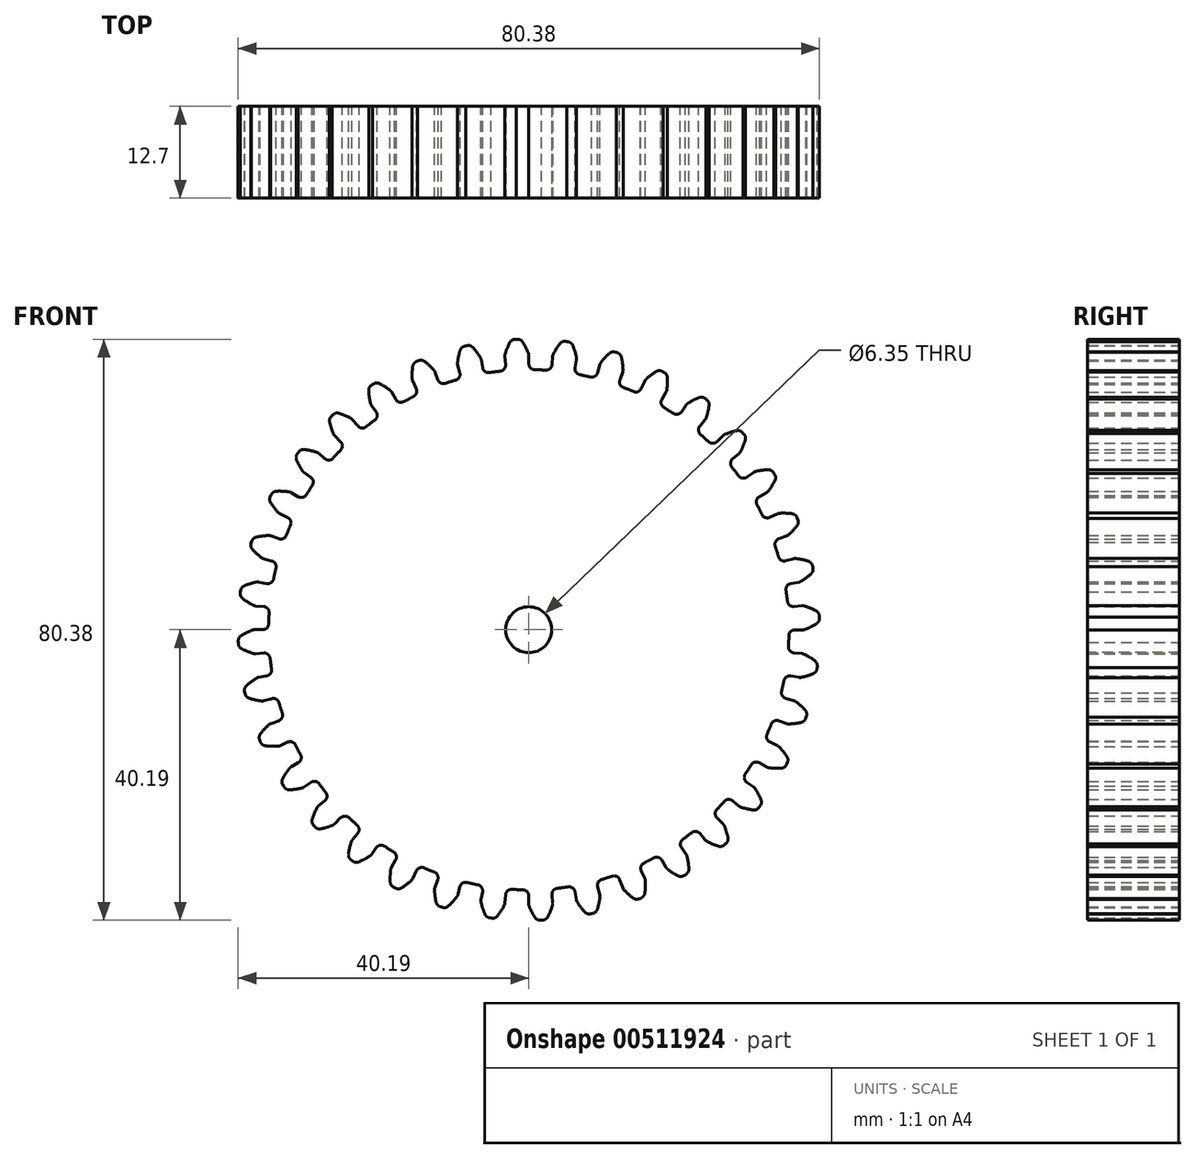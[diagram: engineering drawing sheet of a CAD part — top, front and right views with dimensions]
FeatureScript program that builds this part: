
annotation { "Feature Type Name" : "Feature", "Feature Type Description" : "" }
export const myFeature = defineFeature(function(context is Context, id is Id, definition is map)
    precondition{}
    {
        {
            var Q0;
            Q0=qCreatedBy(makeId("Front.planeOp"),FACE);
            var sketch = newSketch(context, id + "F0", { "sketchPlane" : qUnion([Q0])});
            skArc(sketch, "E0", {"start": v(-3.94, 35.77) * mm, "mid": v(-4.7, 35.68) * mm, "end": v(-5.45, 35.57) * mm});
            skArc(sketch, "E1", {"start": v(-0.05, 38.25) * mm, "mid": v(-0.42, 39.05) * mm, "end": v(-0.85, 39.8) * mm});
            skLineSegment(sketch, "E2", {"start": v(0, 37.94) * mm, "end": v(0, 36.8) * mm});
            skLineSegment(sketch, "E3", {"start": v(-1.58, 40.18) * mm, "end": v(-1.76, 40.18) * mm});
            skLineSegment(sketch, "E4.MirrorCS", {"start": v(-1.93, 40.17) * mm, "end": v(-1.75, 40.18) * mm});
            skArc(sketch, "E5.MirrorCS", {"start": v(-3.28, 38.11) * mm, "mid": v(-2.99, 38.93) * mm, "end": v(-2.62, 39.73) * mm});
            skLineSegment(sketch, "E6.MirrorCS", {"start": v(-3.31, 37.8) * mm, "end": v(-3.21, 36.66) * mm});
            skPoint(sketch, "E7.visualSharp", {"position": v(-3.14, 35.85) * mm});
            skArc(sketch, "E7.filletArc", {"start": v(-3.94, 35.77) * mm, "mid": v(-3.4, 36.07) * mm, "end": v(-3.21, 36.66) * mm});
            skPoint(sketch, "E8.visualSharp", {"position": v(0, 35.98) * mm});
            skArc(sketch, "E8.filletArc", {"start": v(0, 36.8) * mm, "mid": v(0.24, 36.22) * mm, "end": v(0.81, 35.97) * mm});
            skArc(sketch, "E9.filletArc", {"start": v(-1.93, 40.17) * mm, "mid": v(-2.34, 40.04) * mm, "end": v(-2.62, 39.73) * mm});
            skArc(sketch, "E10.filletArc", {"start": v(-0.85, 39.8) * mm, "mid": v(-1.16, 40.1) * mm, "end": v(-1.58, 40.18) * mm});
            skPoint(sketch, "E11.visualSharp", {"position": v(0, 38.1) * mm});
            skArc(sketch, "E11.filletArc", {"start": v(0, 37.94) * mm, "mid": v(0, 38.1) * mm, "end": v(-0.05, 38.25) * mm});
            skPoint(sketch, "E12.visualSharp", {"position": v(-3.33, 37.95) * mm});
            skArc(sketch, "E12.filletArc", {"start": v(-3.28, 38.11) * mm, "mid": v(-3.31, 37.96) * mm, "end": v(-3.31, 37.8) * mm});
            skArc(sketch, "E13.1.0", {"start": v(-10.1, 34.54) * mm, "mid": v(-9.6, 34.93) * mm, "end": v(-9.53, 35.55) * mm});
            skLineSegment(sketch, "E13.1.1", {"start": v(-9.83, 36.65) * mm, "end": v(-9.53, 35.55) * mm});
            skArc(sketch, "E13.1.2", {"start": v(-9.85, 36.96) * mm, "mid": v(-9.85, 36.8) * mm, "end": v(-9.83, 36.65) * mm});
            skArc(sketch, "E13.1.3", {"start": v(-9.85, 36.96) * mm, "mid": v(-9.7, 37.82) * mm, "end": v(-9.48, 38.67) * mm});
            skArc(sketch, "E13.1.4", {"start": v(-8.88, 39.22) * mm, "mid": v(-9.25, 39.03) * mm, "end": v(-9.48, 38.67) * mm});
            skLineSegment(sketch, "E13.1.5", {"start": v(-8.88, 39.22) * mm, "end": v(-8.7, 39.26) * mm});
            skLineSegment(sketch, "E13.1.6", {"start": v(-8.53, 39.3) * mm, "end": v(-8.7, 39.26) * mm});
            skArc(sketch, "E13.1.7", {"start": v(-7.75, 39.05) * mm, "mid": v(-8.1, 39.28) * mm, "end": v(-8.53, 39.3) * mm});
            skArc(sketch, "E13.1.8", {"start": v(-6.7, 37.66) * mm, "mid": v(-7.2, 38.38) * mm, "end": v(-7.75, 39.05) * mm});
            skArc(sketch, "E13.1.9", {"start": v(-6.58, 37.37) * mm, "mid": v(-6.62, 37.52) * mm, "end": v(-6.7, 37.66) * mm});
            skLineSegment(sketch, "E13.1.10", {"start": v(-6.58, 37.37) * mm, "end": v(-6.39, 36.24) * mm});
            skArc(sketch, "E13.1.11", {"start": v(-6.39, 36.24) * mm, "mid": v(-6.06, 35.71) * mm, "end": v(-5.45, 35.57) * mm});
            skArc(sketch, "E13.2.0", {"start": v(-15.94, 32.26) * mm, "mid": v(-15.52, 32.73) * mm, "end": v(-15.56, 33.35) * mm});
            skLineSegment(sketch, "E13.2.1", {"start": v(-16.04, 34.38) * mm, "end": v(-15.56, 33.35) * mm});
            skArc(sketch, "E13.2.2", {"start": v(-16.12, 34.7) * mm, "mid": v(-16.1, 34.53) * mm, "end": v(-16.04, 34.38) * mm});
            skArc(sketch, "E13.2.3", {"start": v(-16.12, 34.7) * mm, "mid": v(-16.13, 35.56) * mm, "end": v(-16.05, 36.43) * mm});
            skArc(sketch, "E13.2.4", {"start": v(-15.55, 37.09) * mm, "mid": v(-15.89, 36.83) * mm, "end": v(-16.05, 36.43) * mm});
            skLineSegment(sketch, "E13.2.5", {"start": v(-15.55, 37.09) * mm, "end": v(-15.39, 37.16) * mm});
            skLineSegment(sketch, "E13.2.6", {"start": v(-15.23, 37.22) * mm, "end": v(-15.4, 37.16) * mm});
            skArc(sketch, "E13.2.7", {"start": v(-14.41, 37.11) * mm, "mid": v(-14.8, 37.28) * mm, "end": v(-15.23, 37.22) * mm});
            skArc(sketch, "E13.2.8", {"start": v(-13.13, 35.93) * mm, "mid": v(-13.75, 36.55) * mm, "end": v(-14.41, 37.11) * mm});
            skArc(sketch, "E13.2.9", {"start": v(-12.97, 35.66) * mm, "mid": v(-13.04, 35.8) * mm, "end": v(-13.13, 35.93) * mm});
            skLineSegment(sketch, "E13.2.10", {"start": v(-12.97, 35.66) * mm, "end": v(-12.58, 34.58) * mm});
            skArc(sketch, "E13.2.11", {"start": v(-12.58, 34.58) * mm, "mid": v(-12.17, 34.12) * mm, "end": v(-11.54, 34.08) * mm});
            skArc(sketch, "E13.3.0", {"start": v(-21.3, 29) * mm, "mid": v(-20.97, 29.54) * mm, "end": v(-21.11, 30.15) * mm});
            skLineSegment(sketch, "E13.3.1", {"start": v(-21.77, 31.08) * mm, "end": v(-21.11, 30.15) * mm});
            skArc(sketch, "E13.3.2", {"start": v(-21.9, 31.37) * mm, "mid": v(-21.85, 31.21) * mm, "end": v(-21.77, 31.08) * mm});
            skArc(sketch, "E13.3.3", {"start": v(-21.9, 31.37) * mm, "mid": v(-22.06, 32.22) * mm, "end": v(-22.13, 33.1) * mm});
            skArc(sketch, "E13.3.4", {"start": v(-21.76, 33.82) * mm, "mid": v(-22.04, 33.5) * mm, "end": v(-22.13, 33.1) * mm});
            skLineSegment(sketch, "E13.3.5", {"start": v(-21.76, 33.82) * mm, "end": v(-21.6, 33.92) * mm});
            skLineSegment(sketch, "E13.3.6", {"start": v(-21.46, 34.01) * mm, "end": v(-21.6, 33.92) * mm});
            skArc(sketch, "E13.3.7", {"start": v(-20.64, 34.05) * mm, "mid": v(-21.05, 34.14) * mm, "end": v(-21.46, 34.01) * mm});
            skArc(sketch, "E13.3.8", {"start": v(-19.17, 33.1) * mm, "mid": v(-19.88, 33.6) * mm, "end": v(-20.64, 34.05) * mm});
            skArc(sketch, "E13.3.9", {"start": v(-18.96, 32.86) * mm, "mid": v(-19.06, 33) * mm, "end": v(-19.17, 33.1) * mm});
            skLineSegment(sketch, "E13.3.10", {"start": v(-18.96, 32.86) * mm, "end": v(-18.4, 31.87) * mm});
            skArc(sketch, "E13.3.11", {"start": v(-18.4, 31.87) * mm, "mid": v(-17.9, 31.49) * mm, "end": v(-17.29, 31.56) * mm});
            skArc(sketch, "E13.4.0", {"start": v(-26.01, 24.86) * mm, "mid": v(-25.78, 25.45) * mm, "end": v(-26.03, 26.02) * mm});
            skLineSegment(sketch, "E13.4.1", {"start": v(-26.83, 26.82) * mm, "end": v(-26.03, 26.02) * mm});
            skArc(sketch, "E13.4.2", {"start": v(-27.01, 27.09) * mm, "mid": v(-26.94, 26.95) * mm, "end": v(-26.83, 26.82) * mm});
            skArc(sketch, "E13.4.3", {"start": v(-27.01, 27.09) * mm, "mid": v(-27.32, 27.9) * mm, "end": v(-27.54, 28.75) * mm});
            skArc(sketch, "E13.4.4", {"start": v(-27.3, 29.53) * mm, "mid": v(-27.53, 29.17) * mm, "end": v(-27.54, 28.75) * mm});
            skLineSegment(sketch, "E13.4.5", {"start": v(-27.3, 29.53) * mm, "end": v(-27.17, 29.65) * mm});
            skLineSegment(sketch, "E13.4.6", {"start": v(-27.04, 29.77) * mm, "end": v(-27.17, 29.65) * mm});
            skArc(sketch, "E13.4.7", {"start": v(-26.24, 29.94) * mm, "mid": v(-26.66, 29.96) * mm, "end": v(-27.04, 29.77) * mm});
            skArc(sketch, "E13.4.8", {"start": v(-24.63, 29.27) * mm, "mid": v(-25.42, 29.64) * mm, "end": v(-26.24, 29.94) * mm});
            skArc(sketch, "E13.4.9", {"start": v(-24.38, 29.07) * mm, "mid": v(-24.5, 29.18) * mm, "end": v(-24.63, 29.27) * mm});
            skLineSegment(sketch, "E13.4.10", {"start": v(-24.38, 29.07) * mm, "end": v(-23.65, 28.2) * mm});
            skArc(sketch, "E13.4.11", {"start": v(-23.65, 28.2) * mm, "mid": v(-23.1, 27.9) * mm, "end": v(-22.5, 28.08) * mm});
            skArc(sketch, "E13.5.0", {"start": v(-29.93, 19.97) * mm, "mid": v(-29.8, 20.58) * mm, "end": v(-30.15, 21.1) * mm});
            skLineSegment(sketch, "E13.5.1", {"start": v(-31.08, 21.76) * mm, "end": v(-30.15, 21.1) * mm});
            skArc(sketch, "E13.5.2", {"start": v(-31.3, 21.98) * mm, "mid": v(-31.2, 21.86) * mm, "end": v(-31.08, 21.76) * mm});
            skArc(sketch, "E13.5.3", {"start": v(-31.3, 21.98) * mm, "mid": v(-31.75, 22.74) * mm, "end": v(-32.12, 23.53) * mm});
            skArc(sketch, "E13.5.4", {"start": v(-32.01, 24.34) * mm, "mid": v(-32.17, 23.95) * mm, "end": v(-32.12, 23.53) * mm});
            skLineSegment(sketch, "E13.5.5", {"start": v(-32.01, 24.34) * mm, "end": v(-31.9, 24.48) * mm});
            skLineSegment(sketch, "E13.5.6", {"start": v(-31.8, 24.62) * mm, "end": v(-31.9, 24.48) * mm});
            skArc(sketch, "E13.5.7", {"start": v(-31.04, 24.93) * mm, "mid": v(-31.46, 24.88) * mm, "end": v(-31.8, 24.62) * mm});
            skArc(sketch, "E13.5.8", {"start": v(-29.34, 24.55) * mm, "mid": v(-30.18, 24.78) * mm, "end": v(-31.04, 24.93) * mm});
            skArc(sketch, "E13.5.9", {"start": v(-29.06, 24.4) * mm, "mid": v(-29.2, 24.49) * mm, "end": v(-29.34, 24.55) * mm});
            skLineSegment(sketch, "E13.5.10", {"start": v(-29.06, 24.4) * mm, "end": v(-28.2, 23.66) * mm});
            skArc(sketch, "E13.5.11", {"start": v(-28.2, 23.66) * mm, "mid": v(-27.6, 23.47) * mm, "end": v(-27.04, 23.74) * mm});
            skArc(sketch, "E13.6.0", {"start": v(-32.95, 14.47) * mm, "mid": v(-32.93, 15.1) * mm, "end": v(-33.36, 15.55) * mm});
            skLineSegment(sketch, "E13.6.1", {"start": v(-34.4, 16.03) * mm, "end": v(-33.36, 15.55) * mm});
            skArc(sketch, "E13.6.2", {"start": v(-34.65, 16.21) * mm, "mid": v(-34.53, 16.1) * mm, "end": v(-34.4, 16.03) * mm});
            skArc(sketch, "E13.6.3", {"start": v(-34.65, 16.21) * mm, "mid": v(-35.21, 16.88) * mm, "end": v(-35.71, 17.6) * mm});
            skArc(sketch, "E13.6.4", {"start": v(-35.75, 18.41) * mm, "mid": v(-35.84, 18) * mm, "end": v(-35.71, 17.6) * mm});
            skLineSegment(sketch, "E13.6.5", {"start": v(-35.75, 18.41) * mm, "end": v(-35.67, 18.57) * mm});
            skLineSegment(sketch, "E13.6.6", {"start": v(-35.59, 18.73) * mm, "end": v(-35.67, 18.57) * mm});
            skArc(sketch, "E13.6.7", {"start": v(-34.9, 19.16) * mm, "mid": v(-35.3, 19.04) * mm, "end": v(-35.59, 18.73) * mm});
            skArc(sketch, "E13.6.8", {"start": v(-33.16, 19.08) * mm, "mid": v(-34.02, 19.16) * mm, "end": v(-34.9, 19.16) * mm});
            skArc(sketch, "E13.6.9", {"start": v(-32.85, 18.98) * mm, "mid": v(-33, 19.04) * mm, "end": v(-33.16, 19.08) * mm});
            skLineSegment(sketch, "E13.6.10", {"start": v(-32.85, 18.98) * mm, "end": v(-31.87, 18.4) * mm});
            skArc(sketch, "E13.6.11", {"start": v(-31.87, 18.4) * mm, "mid": v(-31.25, 18.32) * mm, "end": v(-30.75, 18.69) * mm});
            skArc(sketch, "E13.7.0", {"start": v(-34.96, 8.53) * mm, "mid": v(-35.05, 9.15) * mm, "end": v(-35.55, 9.52) * mm});
            skLineSegment(sketch, "E13.7.1", {"start": v(-36.65, 9.81) * mm, "end": v(-35.55, 9.52) * mm});
            skArc(sketch, "E13.7.2", {"start": v(-36.94, 9.95) * mm, "mid": v(-36.8, 9.87) * mm, "end": v(-36.65, 9.81) * mm});
            skArc(sketch, "E13.7.3", {"start": v(-36.94, 9.95) * mm, "mid": v(-37.6, 10.5) * mm, "end": v(-38.23, 11.12) * mm});
            skArc(sketch, "E13.7.4", {"start": v(-38.4, 11.92) * mm, "mid": v(-38.42, 11.5) * mm, "end": v(-38.23, 11.12) * mm});
            skLineSegment(sketch, "E13.7.5", {"start": v(-38.4, 11.92) * mm, "end": v(-38.36, 12.1) * mm});
            skLineSegment(sketch, "E13.7.6", {"start": v(-38.3, 12.26) * mm, "end": v(-38.36, 12.1) * mm});
            skArc(sketch, "E13.7.7", {"start": v(-37.7, 12.81) * mm, "mid": v(-38.07, 12.62) * mm, "end": v(-38.3, 12.26) * mm});
            skArc(sketch, "E13.7.8", {"start": v(-35.97, 13.03) * mm, "mid": v(-36.83, 12.96) * mm, "end": v(-37.7, 12.81) * mm});
            skArc(sketch, "E13.7.9", {"start": v(-35.65, 12.98) * mm, "mid": v(-35.8, 13.02) * mm, "end": v(-35.97, 13.03) * mm});
            skLineSegment(sketch, "E13.7.10", {"start": v(-35.65, 12.98) * mm, "end": v(-34.58, 12.6) * mm});
            skArc(sketch, "E13.7.11", {"start": v(-34.58, 12.6) * mm, "mid": v(-33.96, 12.61) * mm, "end": v(-33.53, 13.07) * mm});
            skArc(sketch, "E13.8.0", {"start": v(-35.9, 2.33) * mm, "mid": v(-36.1, 2.92) * mm, "end": v(-36.66, 3.2) * mm});
            skLineSegment(sketch, "E13.8.1", {"start": v(-37.8, 3.3) * mm, "end": v(-36.66, 3.2) * mm});
            skArc(sketch, "E13.8.2", {"start": v(-38.1, 3.39) * mm, "mid": v(-37.96, 3.33) * mm, "end": v(-37.8, 3.3) * mm});
            skArc(sketch, "E13.8.3", {"start": v(-38.1, 3.39) * mm, "mid": v(-38.86, 3.82) * mm, "end": v(-39.58, 4.32) * mm});
            skArc(sketch, "E13.8.4", {"start": v(-39.9, 5.07) * mm, "mid": v(-39.84, 4.65) * mm, "end": v(-39.58, 4.32) * mm});
            skLineSegment(sketch, "E13.8.5", {"start": v(-39.9, 5.07) * mm, "end": v(-39.87, 5.25) * mm});
            skLineSegment(sketch, "E13.8.6", {"start": v(-39.85, 5.43) * mm, "end": v(-39.87, 5.25) * mm});
            skArc(sketch, "E13.8.7", {"start": v(-39.35, 6.07) * mm, "mid": v(-39.68, 5.82) * mm, "end": v(-39.85, 5.43) * mm});
            skArc(sketch, "E13.8.8", {"start": v(-37.68, 6.6) * mm, "mid": v(-38.53, 6.37) * mm, "end": v(-39.35, 6.07) * mm});
            skArc(sketch, "E13.8.9", {"start": v(-37.36, 6.6) * mm, "mid": v(-37.52, 6.6) * mm, "end": v(-37.68, 6.6) * mm});
            skLineSegment(sketch, "E13.8.10", {"start": v(-37.36, 6.6) * mm, "end": v(-36.24, 6.4) * mm});
            skArc(sketch, "E13.8.11", {"start": v(-36.24, 6.4) * mm, "mid": v(-35.63, 6.52) * mm, "end": v(-35.29, 7.04) * mm});
            skArc(sketch, "E13.9.0", {"start": v(-35.77, -3.94) * mm, "mid": v(-36.07, -3.4) * mm, "end": v(-36.66, -3.21) * mm});
            skLineSegment(sketch, "E13.9.1", {"start": v(-37.8, -3.31) * mm, "end": v(-36.66, -3.21) * mm});
            skArc(sketch, "E13.9.2", {"start": v(-38.11, -3.28) * mm, "mid": v(-37.96, -3.31) * mm, "end": v(-37.8, -3.31) * mm});
            skArc(sketch, "E13.9.3", {"start": v(-38.11, -3.28) * mm, "mid": v(-38.93, -2.99) * mm, "end": v(-39.73, -2.62) * mm});
            skArc(sketch, "E13.9.4", {"start": v(-40.17, -1.93) * mm, "mid": v(-40.04, -2.34) * mm, "end": v(-39.73, -2.62) * mm});
            skLineSegment(sketch, "E13.9.5", {"start": v(-40.17, -1.93) * mm, "end": v(-40.18, -1.75) * mm});
            skLineSegment(sketch, "E13.9.6", {"start": v(-40.18, -1.58) * mm, "end": v(-40.18, -1.76) * mm});
            skArc(sketch, "E13.9.7", {"start": v(-39.8, -0.85) * mm, "mid": v(-40.1, -1.16) * mm, "end": v(-40.18, -1.58) * mm});
            skArc(sketch, "E13.9.8", {"start": v(-38.25, -0.05) * mm, "mid": v(-39.05, -0.42) * mm, "end": v(-39.8, -0.85) * mm});
            skArc(sketch, "E13.9.9", {"start": v(-37.94, 0) * mm, "mid": v(-38.1, 0) * mm, "end": v(-38.25, -0.05) * mm});
            skLineSegment(sketch, "E13.9.10", {"start": v(-37.94, 0) * mm, "end": v(-36.8, 0) * mm});
            skArc(sketch, "E13.9.11", {"start": v(-36.8, 0) * mm, "mid": v(-36.22, 0.24) * mm, "end": v(-35.97, 0.81) * mm});
            skArc(sketch, "E13.10.0", {"start": v(-34.54, -10.1) * mm, "mid": v(-34.93, -9.6) * mm, "end": v(-35.55, -9.53) * mm});
            skLineSegment(sketch, "E13.10.1", {"start": v(-36.65, -9.83) * mm, "end": v(-35.55, -9.53) * mm});
            skArc(sketch, "E13.10.2", {"start": v(-36.96, -9.85) * mm, "mid": v(-36.8, -9.85) * mm, "end": v(-36.65, -9.83) * mm});
            skArc(sketch, "E13.10.3", {"start": v(-36.96, -9.85) * mm, "mid": v(-37.82, -9.7) * mm, "end": v(-38.67, -9.48) * mm});
            skArc(sketch, "E13.10.4", {"start": v(-39.22, -8.88) * mm, "mid": v(-39.03, -9.25) * mm, "end": v(-38.67, -9.48) * mm});
            skLineSegment(sketch, "E13.10.5", {"start": v(-39.22, -8.88) * mm, "end": v(-39.26, -8.7) * mm});
            skLineSegment(sketch, "E13.10.6", {"start": v(-39.3, -8.53) * mm, "end": v(-39.26, -8.7) * mm});
            skArc(sketch, "E13.10.7", {"start": v(-39.05, -7.75) * mm, "mid": v(-39.28, -8.1) * mm, "end": v(-39.3, -8.53) * mm});
            skArc(sketch, "E13.10.8", {"start": v(-37.66, -6.7) * mm, "mid": v(-38.38, -7.2) * mm, "end": v(-39.05, -7.75) * mm});
            skArc(sketch, "E13.10.9", {"start": v(-37.37, -6.58) * mm, "mid": v(-37.52, -6.62) * mm, "end": v(-37.66, -6.7) * mm});
            skLineSegment(sketch, "E13.10.10", {"start": v(-37.37, -6.58) * mm, "end": v(-36.24, -6.39) * mm});
            skArc(sketch, "E13.10.11", {"start": v(-36.24, -6.39) * mm, "mid": v(-35.71, -6.06) * mm, "end": v(-35.57, -5.45) * mm});
            skArc(sketch, "E13.11.0", {"start": v(-32.26, -15.94) * mm, "mid": v(-32.73, -15.52) * mm, "end": v(-33.35, -15.56) * mm});
            skLineSegment(sketch, "E13.11.1", {"start": v(-34.38, -16.04) * mm, "end": v(-33.35, -15.56) * mm});
            skArc(sketch, "E13.11.2", {"start": v(-34.7, -16.12) * mm, "mid": v(-34.53, -16.1) * mm, "end": v(-34.38, -16.04) * mm});
            skArc(sketch, "E13.11.3", {"start": v(-34.7, -16.12) * mm, "mid": v(-35.56, -16.13) * mm, "end": v(-36.43, -16.05) * mm});
            skArc(sketch, "E13.11.4", {"start": v(-37.09, -15.55) * mm, "mid": v(-36.83, -15.89) * mm, "end": v(-36.43, -16.05) * mm});
            skLineSegment(sketch, "E13.11.5", {"start": v(-37.09, -15.55) * mm, "end": v(-37.16, -15.39) * mm});
            skLineSegment(sketch, "E13.11.6", {"start": v(-37.22, -15.23) * mm, "end": v(-37.16, -15.4) * mm});
            skArc(sketch, "E13.11.7", {"start": v(-37.11, -14.41) * mm, "mid": v(-37.28, -14.8) * mm, "end": v(-37.22, -15.23) * mm});
            skArc(sketch, "E13.11.8", {"start": v(-35.93, -13.13) * mm, "mid": v(-36.55, -13.75) * mm, "end": v(-37.11, -14.41) * mm});
            skArc(sketch, "E13.11.9", {"start": v(-35.66, -12.97) * mm, "mid": v(-35.8, -13.04) * mm, "end": v(-35.93, -13.13) * mm});
            skLineSegment(sketch, "E13.11.10", {"start": v(-35.66, -12.97) * mm, "end": v(-34.58, -12.58) * mm});
            skArc(sketch, "E13.11.11", {"start": v(-34.58, -12.58) * mm, "mid": v(-34.12, -12.17) * mm, "end": v(-34.08, -11.54) * mm});
            skArc(sketch, "E13.12.0", {"start": v(-29, -21.3) * mm, "mid": v(-29.54, -20.97) * mm, "end": v(-30.15, -21.11) * mm});
            skLineSegment(sketch, "E13.12.1", {"start": v(-31.08, -21.77) * mm, "end": v(-30.15, -21.11) * mm});
            skArc(sketch, "E13.12.2", {"start": v(-31.37, -21.9) * mm, "mid": v(-31.21, -21.85) * mm, "end": v(-31.08, -21.77) * mm});
            skArc(sketch, "E13.12.3", {"start": v(-31.37, -21.9) * mm, "mid": v(-32.22, -22.06) * mm, "end": v(-33.1, -22.13) * mm});
            skArc(sketch, "E13.12.4", {"start": v(-33.82, -21.76) * mm, "mid": v(-33.5, -22.04) * mm, "end": v(-33.1, -22.13) * mm});
            skLineSegment(sketch, "E13.12.5", {"start": v(-33.82, -21.76) * mm, "end": v(-33.92, -21.6) * mm});
            skLineSegment(sketch, "E13.12.6", {"start": v(-34.01, -21.46) * mm, "end": v(-33.92, -21.6) * mm});
            skArc(sketch, "E13.12.7", {"start": v(-34.05, -20.64) * mm, "mid": v(-34.14, -21.05) * mm, "end": v(-34.01, -21.46) * mm});
            skArc(sketch, "E13.12.8", {"start": v(-33.1, -19.17) * mm, "mid": v(-33.6, -19.88) * mm, "end": v(-34.05, -20.64) * mm});
            skArc(sketch, "E13.12.9", {"start": v(-32.86, -18.96) * mm, "mid": v(-33, -19.06) * mm, "end": v(-33.1, -19.17) * mm});
            skLineSegment(sketch, "E13.12.10", {"start": v(-32.86, -18.96) * mm, "end": v(-31.87, -18.4) * mm});
            skArc(sketch, "E13.12.11", {"start": v(-31.87, -18.4) * mm, "mid": v(-31.49, -17.9) * mm, "end": v(-31.56, -17.29) * mm});
            skArc(sketch, "E13.13.0", {"start": v(-24.86, -26.01) * mm, "mid": v(-25.45, -25.78) * mm, "end": v(-26.02, -26.03) * mm});
            skLineSegment(sketch, "E13.13.1", {"start": v(-26.82, -26.83) * mm, "end": v(-26.02, -26.03) * mm});
            skArc(sketch, "E13.13.2", {"start": v(-27.09, -27.01) * mm, "mid": v(-26.95, -26.94) * mm, "end": v(-26.82, -26.83) * mm});
            skArc(sketch, "E13.13.3", {"start": v(-27.09, -27.01) * mm, "mid": v(-27.9, -27.32) * mm, "end": v(-28.75, -27.54) * mm});
            skArc(sketch, "E13.13.4", {"start": v(-29.53, -27.3) * mm, "mid": v(-29.17, -27.53) * mm, "end": v(-28.75, -27.54) * mm});
            skLineSegment(sketch, "E13.13.5", {"start": v(-29.53, -27.3) * mm, "end": v(-29.65, -27.17) * mm});
            skLineSegment(sketch, "E13.13.6", {"start": v(-29.77, -27.04) * mm, "end": v(-29.65, -27.17) * mm});
            skArc(sketch, "E13.13.7", {"start": v(-29.94, -26.24) * mm, "mid": v(-29.96, -26.66) * mm, "end": v(-29.77, -27.04) * mm});
            skArc(sketch, "E13.13.8", {"start": v(-29.27, -24.63) * mm, "mid": v(-29.64, -25.42) * mm, "end": v(-29.94, -26.24) * mm});
            skArc(sketch, "E13.13.9", {"start": v(-29.07, -24.38) * mm, "mid": v(-29.18, -24.5) * mm, "end": v(-29.27, -24.63) * mm});
            skLineSegment(sketch, "E13.13.10", {"start": v(-29.07, -24.38) * mm, "end": v(-28.2, -23.65) * mm});
            skArc(sketch, "E13.13.11", {"start": v(-28.2, -23.65) * mm, "mid": v(-27.9, -23.1) * mm, "end": v(-28.08, -22.5) * mm});
            skArc(sketch, "E13.14.0", {"start": v(-19.97, -29.93) * mm, "mid": v(-20.58, -29.8) * mm, "end": v(-21.1, -30.15) * mm});
            skLineSegment(sketch, "E13.14.1", {"start": v(-21.76, -31.08) * mm, "end": v(-21.1, -30.15) * mm});
            skArc(sketch, "E13.14.2", {"start": v(-21.98, -31.3) * mm, "mid": v(-21.86, -31.2) * mm, "end": v(-21.76, -31.08) * mm});
            skArc(sketch, "E13.14.3", {"start": v(-21.98, -31.3) * mm, "mid": v(-22.74, -31.75) * mm, "end": v(-23.53, -32.12) * mm});
            skArc(sketch, "E13.14.4", {"start": v(-24.34, -32.01) * mm, "mid": v(-23.95, -32.17) * mm, "end": v(-23.53, -32.12) * mm});
            skLineSegment(sketch, "E13.14.5", {"start": v(-24.34, -32.01) * mm, "end": v(-24.48, -31.9) * mm});
            skLineSegment(sketch, "E13.14.6", {"start": v(-24.62, -31.8) * mm, "end": v(-24.48, -31.9) * mm});
            skArc(sketch, "E13.14.7", {"start": v(-24.93, -31.04) * mm, "mid": v(-24.88, -31.46) * mm, "end": v(-24.62, -31.8) * mm});
            skArc(sketch, "E13.14.8", {"start": v(-24.55, -29.34) * mm, "mid": v(-24.78, -30.18) * mm, "end": v(-24.93, -31.04) * mm});
            skArc(sketch, "E13.14.9", {"start": v(-24.4, -29.06) * mm, "mid": v(-24.49, -29.2) * mm, "end": v(-24.55, -29.34) * mm});
            skLineSegment(sketch, "E13.14.10", {"start": v(-24.4, -29.06) * mm, "end": v(-23.66, -28.2) * mm});
            skArc(sketch, "E13.14.11", {"start": v(-23.66, -28.2) * mm, "mid": v(-23.47, -27.6) * mm, "end": v(-23.74, -27.04) * mm});
            skArc(sketch, "E13.15.0", {"start": v(-14.47, -32.95) * mm, "mid": v(-15.1, -32.93) * mm, "end": v(-15.55, -33.36) * mm});
            skLineSegment(sketch, "E13.15.1", {"start": v(-16.03, -34.4) * mm, "end": v(-15.55, -33.36) * mm});
            skArc(sketch, "E13.15.2", {"start": v(-16.21, -34.65) * mm, "mid": v(-16.1, -34.53) * mm, "end": v(-16.03, -34.4) * mm});
            skArc(sketch, "E13.15.3", {"start": v(-16.21, -34.65) * mm, "mid": v(-16.88, -35.21) * mm, "end": v(-17.6, -35.71) * mm});
            skArc(sketch, "E13.15.4", {"start": v(-18.41, -35.75) * mm, "mid": v(-18, -35.84) * mm, "end": v(-17.6, -35.71) * mm});
            skLineSegment(sketch, "E13.15.5", {"start": v(-18.41, -35.75) * mm, "end": v(-18.57, -35.67) * mm});
            skLineSegment(sketch, "E13.15.6", {"start": v(-18.73, -35.59) * mm, "end": v(-18.57, -35.67) * mm});
            skArc(sketch, "E13.15.7", {"start": v(-19.16, -34.9) * mm, "mid": v(-19.04, -35.3) * mm, "end": v(-18.73, -35.59) * mm});
            skArc(sketch, "E13.15.8", {"start": v(-19.08, -33.16) * mm, "mid": v(-19.16, -34.02) * mm, "end": v(-19.16, -34.9) * mm});
            skArc(sketch, "E13.15.9", {"start": v(-18.98, -32.85) * mm, "mid": v(-19.04, -33) * mm, "end": v(-19.08, -33.16) * mm});
            skLineSegment(sketch, "E13.15.10", {"start": v(-18.98, -32.85) * mm, "end": v(-18.4, -31.87) * mm});
            skArc(sketch, "E13.15.11", {"start": v(-18.4, -31.87) * mm, "mid": v(-18.32, -31.25) * mm, "end": v(-18.69, -30.75) * mm});
            skArc(sketch, "E13.16.0", {"start": v(-8.53, -34.96) * mm, "mid": v(-9.15, -35.05) * mm, "end": v(-9.52, -35.55) * mm});
            skLineSegment(sketch, "E13.16.1", {"start": v(-9.81, -36.65) * mm, "end": v(-9.52, -35.55) * mm});
            skArc(sketch, "E13.16.2", {"start": v(-9.95, -36.94) * mm, "mid": v(-9.87, -36.8) * mm, "end": v(-9.81, -36.65) * mm});
            skArc(sketch, "E13.16.3", {"start": v(-9.95, -36.94) * mm, "mid": v(-10.5, -37.6) * mm, "end": v(-11.12, -38.23) * mm});
            skArc(sketch, "E13.16.4", {"start": v(-11.92, -38.4) * mm, "mid": v(-11.5, -38.42) * mm, "end": v(-11.12, -38.23) * mm});
            skLineSegment(sketch, "E13.16.5", {"start": v(-11.92, -38.4) * mm, "end": v(-12.1, -38.36) * mm});
            skLineSegment(sketch, "E13.16.6", {"start": v(-12.26, -38.3) * mm, "end": v(-12.1, -38.36) * mm});
            skArc(sketch, "E13.16.7", {"start": v(-12.81, -37.7) * mm, "mid": v(-12.62, -38.07) * mm, "end": v(-12.26, -38.3) * mm});
            skArc(sketch, "E13.16.8", {"start": v(-13.03, -35.97) * mm, "mid": v(-12.96, -36.83) * mm, "end": v(-12.81, -37.7) * mm});
            skArc(sketch, "E13.16.9", {"start": v(-12.98, -35.65) * mm, "mid": v(-13.02, -35.8) * mm, "end": v(-13.03, -35.97) * mm});
            skLineSegment(sketch, "E13.16.10", {"start": v(-12.98, -35.65) * mm, "end": v(-12.6, -34.58) * mm});
            skArc(sketch, "E13.16.11", {"start": v(-12.6, -34.58) * mm, "mid": v(-12.61, -33.96) * mm, "end": v(-13.07, -33.53) * mm});
            skArc(sketch, "E13.17.0", {"start": v(-2.33, -35.9) * mm, "mid": v(-2.92, -36.1) * mm, "end": v(-3.2, -36.66) * mm});
            skLineSegment(sketch, "E13.17.1", {"start": v(-3.3, -37.8) * mm, "end": v(-3.2, -36.66) * mm});
            skArc(sketch, "E13.17.2", {"start": v(-3.39, -38.1) * mm, "mid": v(-3.33, -37.96) * mm, "end": v(-3.3, -37.8) * mm});
            skArc(sketch, "E13.17.3", {"start": v(-3.39, -38.1) * mm, "mid": v(-3.82, -38.86) * mm, "end": v(-4.32, -39.58) * mm});
            skArc(sketch, "E13.17.4", {"start": v(-5.07, -39.9) * mm, "mid": v(-4.65, -39.84) * mm, "end": v(-4.32, -39.58) * mm});
            skLineSegment(sketch, "E13.17.5", {"start": v(-5.07, -39.9) * mm, "end": v(-5.25, -39.87) * mm});
            skLineSegment(sketch, "E13.17.6", {"start": v(-5.43, -39.85) * mm, "end": v(-5.25, -39.87) * mm});
            skArc(sketch, "E13.17.7", {"start": v(-6.07, -39.35) * mm, "mid": v(-5.82, -39.68) * mm, "end": v(-5.43, -39.85) * mm});
            skArc(sketch, "E13.17.8", {"start": v(-6.6, -37.68) * mm, "mid": v(-6.37, -38.53) * mm, "end": v(-6.07, -39.35) * mm});
            skArc(sketch, "E13.17.9", {"start": v(-6.6, -37.36) * mm, "mid": v(-6.6, -37.52) * mm, "end": v(-6.6, -37.68) * mm});
            skLineSegment(sketch, "E13.17.10", {"start": v(-6.6, -37.36) * mm, "end": v(-6.4, -36.24) * mm});
            skArc(sketch, "E13.17.11", {"start": v(-6.4, -36.24) * mm, "mid": v(-6.52, -35.63) * mm, "end": v(-7.04, -35.29) * mm});
            skArc(sketch, "E13.18.0", {"start": v(3.94, -35.77) * mm, "mid": v(3.4, -36.07) * mm, "end": v(3.21, -36.66) * mm});
            skLineSegment(sketch, "E13.18.1", {"start": v(3.31, -37.8) * mm, "end": v(3.21, -36.66) * mm});
            skArc(sketch, "E13.18.2", {"start": v(3.28, -38.11) * mm, "mid": v(3.31, -37.96) * mm, "end": v(3.31, -37.8) * mm});
            skArc(sketch, "E13.18.3", {"start": v(3.28, -38.11) * mm, "mid": v(2.99, -38.93) * mm, "end": v(2.62, -39.73) * mm});
            skArc(sketch, "E13.18.4", {"start": v(1.93, -40.17) * mm, "mid": v(2.34, -40.04) * mm, "end": v(2.62, -39.73) * mm});
            skLineSegment(sketch, "E13.18.5", {"start": v(1.93, -40.17) * mm, "end": v(1.75, -40.18) * mm});
            skLineSegment(sketch, "E13.18.6", {"start": v(1.58, -40.18) * mm, "end": v(1.76, -40.18) * mm});
            skArc(sketch, "E13.18.7", {"start": v(0.85, -39.8) * mm, "mid": v(1.16, -40.1) * mm, "end": v(1.58, -40.18) * mm});
            skArc(sketch, "E13.18.8", {"start": v(0.05, -38.25) * mm, "mid": v(0.42, -39.05) * mm, "end": v(0.85, -39.8) * mm});
            skArc(sketch, "E13.18.9", {"start": v(0, -37.94) * mm, "mid": v(0, -38.1) * mm, "end": v(0.05, -38.25) * mm});
            skLineSegment(sketch, "E13.18.10", {"start": v(0, -37.94) * mm, "end": v(0, -36.8) * mm});
            skArc(sketch, "E13.18.11", {"start": v(0, -36.8) * mm, "mid": v(-0.24, -36.22) * mm, "end": v(-0.81, -35.97) * mm});
            skArc(sketch, "E13.19.0", {"start": v(10.1, -34.54) * mm, "mid": v(9.6, -34.93) * mm, "end": v(9.53, -35.55) * mm});
            skLineSegment(sketch, "E13.19.1", {"start": v(9.83, -36.65) * mm, "end": v(9.53, -35.55) * mm});
            skArc(sketch, "E13.19.2", {"start": v(9.85, -36.96) * mm, "mid": v(9.85, -36.8) * mm, "end": v(9.83, -36.65) * mm});
            skArc(sketch, "E13.19.3", {"start": v(9.85, -36.96) * mm, "mid": v(9.7, -37.82) * mm, "end": v(9.48, -38.67) * mm});
            skArc(sketch, "E13.19.4", {"start": v(8.88, -39.22) * mm, "mid": v(9.25, -39.03) * mm, "end": v(9.48, -38.67) * mm});
            skLineSegment(sketch, "E13.19.5", {"start": v(8.88, -39.22) * mm, "end": v(8.7, -39.26) * mm});
            skLineSegment(sketch, "E13.19.6", {"start": v(8.53, -39.3) * mm, "end": v(8.7, -39.26) * mm});
            skArc(sketch, "E13.19.7", {"start": v(7.75, -39.05) * mm, "mid": v(8.1, -39.28) * mm, "end": v(8.53, -39.3) * mm});
            skArc(sketch, "E13.19.8", {"start": v(6.7, -37.66) * mm, "mid": v(7.2, -38.38) * mm, "end": v(7.75, -39.05) * mm});
            skArc(sketch, "E13.19.9", {"start": v(6.58, -37.37) * mm, "mid": v(6.62, -37.52) * mm, "end": v(6.7, -37.66) * mm});
            skLineSegment(sketch, "E13.19.10", {"start": v(6.58, -37.37) * mm, "end": v(6.39, -36.24) * mm});
            skArc(sketch, "E13.19.11", {"start": v(6.39, -36.24) * mm, "mid": v(6.06, -35.71) * mm, "end": v(5.45, -35.57) * mm});
            skArc(sketch, "E13.20.0", {"start": v(15.94, -32.26) * mm, "mid": v(15.52, -32.73) * mm, "end": v(15.56, -33.35) * mm});
            skLineSegment(sketch, "E13.20.1", {"start": v(16.04, -34.38) * mm, "end": v(15.56, -33.35) * mm});
            skArc(sketch, "E13.20.2", {"start": v(16.12, -34.7) * mm, "mid": v(16.1, -34.53) * mm, "end": v(16.04, -34.38) * mm});
            skArc(sketch, "E13.20.3", {"start": v(16.12, -34.7) * mm, "mid": v(16.13, -35.56) * mm, "end": v(16.05, -36.43) * mm});
            skArc(sketch, "E13.20.4", {"start": v(15.55, -37.09) * mm, "mid": v(15.89, -36.83) * mm, "end": v(16.05, -36.43) * mm});
            skLineSegment(sketch, "E13.20.5", {"start": v(15.55, -37.09) * mm, "end": v(15.39, -37.16) * mm});
            skLineSegment(sketch, "E13.20.6", {"start": v(15.23, -37.22) * mm, "end": v(15.4, -37.16) * mm});
            skArc(sketch, "E13.20.7", {"start": v(14.41, -37.11) * mm, "mid": v(14.8, -37.28) * mm, "end": v(15.23, -37.22) * mm});
            skArc(sketch, "E13.20.8", {"start": v(13.13, -35.93) * mm, "mid": v(13.75, -36.55) * mm, "end": v(14.41, -37.11) * mm});
            skArc(sketch, "E13.20.9", {"start": v(12.97, -35.66) * mm, "mid": v(13.04, -35.8) * mm, "end": v(13.13, -35.93) * mm});
            skLineSegment(sketch, "E13.20.10", {"start": v(12.97, -35.66) * mm, "end": v(12.58, -34.58) * mm});
            skArc(sketch, "E13.20.11", {"start": v(12.58, -34.58) * mm, "mid": v(12.17, -34.12) * mm, "end": v(11.54, -34.08) * mm});
            skArc(sketch, "E13.21.0", {"start": v(21.3, -29) * mm, "mid": v(20.97, -29.54) * mm, "end": v(21.11, -30.15) * mm});
            skLineSegment(sketch, "E13.21.1", {"start": v(21.77, -31.08) * mm, "end": v(21.11, -30.15) * mm});
            skArc(sketch, "E13.21.2", {"start": v(21.9, -31.37) * mm, "mid": v(21.85, -31.21) * mm, "end": v(21.77, -31.08) * mm});
            skArc(sketch, "E13.21.3", {"start": v(21.9, -31.37) * mm, "mid": v(22.06, -32.22) * mm, "end": v(22.13, -33.1) * mm});
            skArc(sketch, "E13.21.4", {"start": v(21.76, -33.82) * mm, "mid": v(22.04, -33.5) * mm, "end": v(22.13, -33.1) * mm});
            skLineSegment(sketch, "E13.21.5", {"start": v(21.76, -33.82) * mm, "end": v(21.6, -33.92) * mm});
            skLineSegment(sketch, "E13.21.6", {"start": v(21.46, -34.01) * mm, "end": v(21.6, -33.92) * mm});
            skArc(sketch, "E13.21.7", {"start": v(20.64, -34.05) * mm, "mid": v(21.05, -34.14) * mm, "end": v(21.46, -34.01) * mm});
            skArc(sketch, "E13.21.8", {"start": v(19.17, -33.1) * mm, "mid": v(19.88, -33.6) * mm, "end": v(20.64, -34.05) * mm});
            skArc(sketch, "E13.21.9", {"start": v(18.96, -32.86) * mm, "mid": v(19.06, -33) * mm, "end": v(19.17, -33.1) * mm});
            skLineSegment(sketch, "E13.21.10", {"start": v(18.96, -32.86) * mm, "end": v(18.4, -31.87) * mm});
            skArc(sketch, "E13.21.11", {"start": v(18.4, -31.87) * mm, "mid": v(17.9, -31.49) * mm, "end": v(17.29, -31.56) * mm});
            skArc(sketch, "E13.22.0", {"start": v(26.01, -24.86) * mm, "mid": v(25.78, -25.45) * mm, "end": v(26.03, -26.02) * mm});
            skLineSegment(sketch, "E13.22.1", {"start": v(26.83, -26.82) * mm, "end": v(26.03, -26.02) * mm});
            skArc(sketch, "E13.22.2", {"start": v(27.01, -27.09) * mm, "mid": v(26.94, -26.95) * mm, "end": v(26.83, -26.82) * mm});
            skArc(sketch, "E13.22.3", {"start": v(27.01, -27.09) * mm, "mid": v(27.32, -27.9) * mm, "end": v(27.54, -28.75) * mm});
            skArc(sketch, "E13.22.4", {"start": v(27.3, -29.53) * mm, "mid": v(27.53, -29.17) * mm, "end": v(27.54, -28.75) * mm});
            skLineSegment(sketch, "E13.22.5", {"start": v(27.3, -29.53) * mm, "end": v(27.17, -29.65) * mm});
            skLineSegment(sketch, "E13.22.6", {"start": v(27.04, -29.77) * mm, "end": v(27.17, -29.65) * mm});
            skArc(sketch, "E13.22.7", {"start": v(26.24, -29.94) * mm, "mid": v(26.66, -29.96) * mm, "end": v(27.04, -29.77) * mm});
            skArc(sketch, "E13.22.8", {"start": v(24.63, -29.27) * mm, "mid": v(25.42, -29.64) * mm, "end": v(26.24, -29.94) * mm});
            skArc(sketch, "E13.22.9", {"start": v(24.38, -29.07) * mm, "mid": v(24.5, -29.18) * mm, "end": v(24.63, -29.27) * mm});
            skLineSegment(sketch, "E13.22.10", {"start": v(24.38, -29.07) * mm, "end": v(23.65, -28.2) * mm});
            skArc(sketch, "E13.22.11", {"start": v(23.65, -28.2) * mm, "mid": v(23.1, -27.9) * mm, "end": v(22.5, -28.08) * mm});
            skArc(sketch, "E13.23.0", {"start": v(29.93, -19.97) * mm, "mid": v(29.8, -20.58) * mm, "end": v(30.15, -21.1) * mm});
            skLineSegment(sketch, "E13.23.1", {"start": v(31.08, -21.76) * mm, "end": v(30.15, -21.1) * mm});
            skArc(sketch, "E13.23.2", {"start": v(31.3, -21.98) * mm, "mid": v(31.2, -21.86) * mm, "end": v(31.08, -21.76) * mm});
            skArc(sketch, "E13.23.3", {"start": v(31.3, -21.98) * mm, "mid": v(31.75, -22.74) * mm, "end": v(32.12, -23.53) * mm});
            skArc(sketch, "E13.23.4", {"start": v(32.01, -24.34) * mm, "mid": v(32.17, -23.95) * mm, "end": v(32.12, -23.53) * mm});
            skLineSegment(sketch, "E13.23.5", {"start": v(32.01, -24.34) * mm, "end": v(31.9, -24.48) * mm});
            skLineSegment(sketch, "E13.23.6", {"start": v(31.8, -24.62) * mm, "end": v(31.9, -24.48) * mm});
            skArc(sketch, "E13.23.7", {"start": v(31.04, -24.93) * mm, "mid": v(31.46, -24.88) * mm, "end": v(31.8, -24.62) * mm});
            skArc(sketch, "E13.23.8", {"start": v(29.34, -24.55) * mm, "mid": v(30.18, -24.78) * mm, "end": v(31.04, -24.93) * mm});
            skArc(sketch, "E13.23.9", {"start": v(29.06, -24.4) * mm, "mid": v(29.2, -24.49) * mm, "end": v(29.34, -24.55) * mm});
            skLineSegment(sketch, "E13.23.10", {"start": v(29.06, -24.4) * mm, "end": v(28.2, -23.66) * mm});
            skArc(sketch, "E13.23.11", {"start": v(28.2, -23.66) * mm, "mid": v(27.6, -23.47) * mm, "end": v(27.04, -23.74) * mm});
            skArc(sketch, "E13.24.0", {"start": v(32.95, -14.47) * mm, "mid": v(32.93, -15.1) * mm, "end": v(33.36, -15.55) * mm});
            skLineSegment(sketch, "E13.24.1", {"start": v(34.4, -16.03) * mm, "end": v(33.36, -15.55) * mm});
            skArc(sketch, "E13.24.2", {"start": v(34.65, -16.21) * mm, "mid": v(34.53, -16.1) * mm, "end": v(34.4, -16.03) * mm});
            skArc(sketch, "E13.24.3", {"start": v(34.65, -16.21) * mm, "mid": v(35.21, -16.88) * mm, "end": v(35.71, -17.6) * mm});
            skArc(sketch, "E13.24.4", {"start": v(35.75, -18.41) * mm, "mid": v(35.84, -18) * mm, "end": v(35.71, -17.6) * mm});
            skLineSegment(sketch, "E13.24.5", {"start": v(35.75, -18.41) * mm, "end": v(35.67, -18.57) * mm});
            skLineSegment(sketch, "E13.24.6", {"start": v(35.59, -18.73) * mm, "end": v(35.67, -18.57) * mm});
            skArc(sketch, "E13.24.7", {"start": v(34.9, -19.16) * mm, "mid": v(35.3, -19.04) * mm, "end": v(35.59, -18.73) * mm});
            skArc(sketch, "E13.24.8", {"start": v(33.16, -19.08) * mm, "mid": v(34.02, -19.16) * mm, "end": v(34.9, -19.16) * mm});
            skArc(sketch, "E13.24.9", {"start": v(32.85, -18.98) * mm, "mid": v(33, -19.04) * mm, "end": v(33.16, -19.08) * mm});
            skLineSegment(sketch, "E13.24.10", {"start": v(32.85, -18.98) * mm, "end": v(31.87, -18.4) * mm});
            skArc(sketch, "E13.24.11", {"start": v(31.87, -18.4) * mm, "mid": v(31.25, -18.32) * mm, "end": v(30.75, -18.69) * mm});
            skArc(sketch, "E13.25.0", {"start": v(34.96, -8.53) * mm, "mid": v(35.05, -9.15) * mm, "end": v(35.55, -9.52) * mm});
            skLineSegment(sketch, "E13.25.1", {"start": v(36.65, -9.81) * mm, "end": v(35.55, -9.52) * mm});
            skArc(sketch, "E13.25.2", {"start": v(36.94, -9.95) * mm, "mid": v(36.8, -9.87) * mm, "end": v(36.65, -9.81) * mm});
            skArc(sketch, "E13.25.3", {"start": v(36.94, -9.95) * mm, "mid": v(37.6, -10.5) * mm, "end": v(38.23, -11.12) * mm});
            skArc(sketch, "E13.25.4", {"start": v(38.4, -11.92) * mm, "mid": v(38.42, -11.5) * mm, "end": v(38.23, -11.12) * mm});
            skLineSegment(sketch, "E13.25.5", {"start": v(38.4, -11.92) * mm, "end": v(38.36, -12.1) * mm});
            skLineSegment(sketch, "E13.25.6", {"start": v(38.3, -12.26) * mm, "end": v(38.36, -12.1) * mm});
            skArc(sketch, "E13.25.7", {"start": v(37.7, -12.81) * mm, "mid": v(38.07, -12.62) * mm, "end": v(38.3, -12.26) * mm});
            skArc(sketch, "E13.25.8", {"start": v(35.97, -13.03) * mm, "mid": v(36.83, -12.96) * mm, "end": v(37.7, -12.81) * mm});
            skArc(sketch, "E13.25.9", {"start": v(35.65, -12.98) * mm, "mid": v(35.8, -13.02) * mm, "end": v(35.97, -13.03) * mm});
            skLineSegment(sketch, "E13.25.10", {"start": v(35.65, -12.98) * mm, "end": v(34.58, -12.6) * mm});
            skArc(sketch, "E13.25.11", {"start": v(34.58, -12.6) * mm, "mid": v(33.96, -12.61) * mm, "end": v(33.53, -13.07) * mm});
            skArc(sketch, "E13.26.0", {"start": v(35.9, -2.33) * mm, "mid": v(36.1, -2.92) * mm, "end": v(36.66, -3.2) * mm});
            skLineSegment(sketch, "E13.26.1", {"start": v(37.8, -3.3) * mm, "end": v(36.66, -3.2) * mm});
            skArc(sketch, "E13.26.2", {"start": v(38.1, -3.39) * mm, "mid": v(37.96, -3.33) * mm, "end": v(37.8, -3.3) * mm});
            skArc(sketch, "E13.26.3", {"start": v(38.1, -3.39) * mm, "mid": v(38.86, -3.82) * mm, "end": v(39.58, -4.32) * mm});
            skArc(sketch, "E13.26.4", {"start": v(39.9, -5.07) * mm, "mid": v(39.84, -4.65) * mm, "end": v(39.58, -4.32) * mm});
            skLineSegment(sketch, "E13.26.5", {"start": v(39.9, -5.07) * mm, "end": v(39.87, -5.25) * mm});
            skLineSegment(sketch, "E13.26.6", {"start": v(39.85, -5.43) * mm, "end": v(39.87, -5.25) * mm});
            skArc(sketch, "E13.26.7", {"start": v(39.35, -6.07) * mm, "mid": v(39.68, -5.82) * mm, "end": v(39.85, -5.43) * mm});
            skArc(sketch, "E13.26.8", {"start": v(37.68, -6.6) * mm, "mid": v(38.53, -6.37) * mm, "end": v(39.35, -6.07) * mm});
            skArc(sketch, "E13.26.9", {"start": v(37.36, -6.6) * mm, "mid": v(37.52, -6.6) * mm, "end": v(37.68, -6.6) * mm});
            skLineSegment(sketch, "E13.26.10", {"start": v(37.36, -6.6) * mm, "end": v(36.24, -6.4) * mm});
            skArc(sketch, "E13.26.11", {"start": v(36.24, -6.4) * mm, "mid": v(35.63, -6.52) * mm, "end": v(35.29, -7.04) * mm});
            skArc(sketch, "E13.27.0", {"start": v(35.77, 3.94) * mm, "mid": v(36.07, 3.4) * mm, "end": v(36.66, 3.21) * mm});
            skLineSegment(sketch, "E13.27.1", {"start": v(37.8, 3.31) * mm, "end": v(36.66, 3.21) * mm});
            skArc(sketch, "E13.27.2", {"start": v(38.11, 3.28) * mm, "mid": v(37.96, 3.31) * mm, "end": v(37.8, 3.31) * mm});
            skArc(sketch, "E13.27.3", {"start": v(38.11, 3.28) * mm, "mid": v(38.93, 2.99) * mm, "end": v(39.73, 2.62) * mm});
            skArc(sketch, "E13.27.4", {"start": v(40.17, 1.93) * mm, "mid": v(40.04, 2.34) * mm, "end": v(39.73, 2.62) * mm});
            skLineSegment(sketch, "E13.27.5", {"start": v(40.17, 1.93) * mm, "end": v(40.18, 1.75) * mm});
            skLineSegment(sketch, "E13.27.6", {"start": v(40.18, 1.58) * mm, "end": v(40.18, 1.76) * mm});
            skArc(sketch, "E13.27.7", {"start": v(39.8, 0.85) * mm, "mid": v(40.1, 1.16) * mm, "end": v(40.18, 1.58) * mm});
            skArc(sketch, "E13.27.8", {"start": v(38.25, 0.05) * mm, "mid": v(39.05, 0.42) * mm, "end": v(39.8, 0.85) * mm});
            skArc(sketch, "E13.27.9", {"start": v(37.94, 0) * mm, "mid": v(38.1, 0) * mm, "end": v(38.25, 0.05) * mm});
            skLineSegment(sketch, "E13.27.10", {"start": v(37.94, 0) * mm, "end": v(36.8, 0) * mm});
            skArc(sketch, "E13.27.11", {"start": v(36.8, 0) * mm, "mid": v(36.22, -0.24) * mm, "end": v(35.97, -0.81) * mm});
            skArc(sketch, "E13.28.0", {"start": v(34.54, 10.1) * mm, "mid": v(34.93, 9.6) * mm, "end": v(35.55, 9.53) * mm});
            skLineSegment(sketch, "E13.28.1", {"start": v(36.65, 9.83) * mm, "end": v(35.55, 9.53) * mm});
            skArc(sketch, "E13.28.2", {"start": v(36.96, 9.85) * mm, "mid": v(36.8, 9.85) * mm, "end": v(36.65, 9.83) * mm});
            skArc(sketch, "E13.28.3", {"start": v(36.96, 9.85) * mm, "mid": v(37.82, 9.7) * mm, "end": v(38.67, 9.48) * mm});
            skArc(sketch, "E13.28.4", {"start": v(39.22, 8.88) * mm, "mid": v(39.03, 9.25) * mm, "end": v(38.67, 9.48) * mm});
            skLineSegment(sketch, "E13.28.5", {"start": v(39.22, 8.88) * mm, "end": v(39.26, 8.7) * mm});
            skLineSegment(sketch, "E13.28.6", {"start": v(39.3, 8.53) * mm, "end": v(39.26, 8.7) * mm});
            skArc(sketch, "E13.28.7", {"start": v(39.05, 7.75) * mm, "mid": v(39.28, 8.1) * mm, "end": v(39.3, 8.53) * mm});
            skArc(sketch, "E13.28.8", {"start": v(37.66, 6.7) * mm, "mid": v(38.38, 7.2) * mm, "end": v(39.05, 7.75) * mm});
            skArc(sketch, "E13.28.9", {"start": v(37.37, 6.58) * mm, "mid": v(37.52, 6.62) * mm, "end": v(37.66, 6.7) * mm});
            skLineSegment(sketch, "E13.28.10", {"start": v(37.37, 6.58) * mm, "end": v(36.24, 6.39) * mm});
            skArc(sketch, "E13.28.11", {"start": v(36.24, 6.39) * mm, "mid": v(35.71, 6.06) * mm, "end": v(35.57, 5.45) * mm});
            skArc(sketch, "E13.29.0", {"start": v(32.26, 15.94) * mm, "mid": v(32.73, 15.52) * mm, "end": v(33.35, 15.56) * mm});
            skLineSegment(sketch, "E13.29.1", {"start": v(34.38, 16.04) * mm, "end": v(33.35, 15.56) * mm});
            skArc(sketch, "E13.29.2", {"start": v(34.7, 16.12) * mm, "mid": v(34.53, 16.1) * mm, "end": v(34.38, 16.04) * mm});
            skArc(sketch, "E13.29.3", {"start": v(34.7, 16.12) * mm, "mid": v(35.56, 16.13) * mm, "end": v(36.43, 16.05) * mm});
            skArc(sketch, "E13.29.4", {"start": v(37.09, 15.55) * mm, "mid": v(36.83, 15.89) * mm, "end": v(36.43, 16.05) * mm});
            skLineSegment(sketch, "E13.29.5", {"start": v(37.09, 15.55) * mm, "end": v(37.16, 15.39) * mm});
            skLineSegment(sketch, "E13.29.6", {"start": v(37.22, 15.23) * mm, "end": v(37.16, 15.4) * mm});
            skArc(sketch, "E13.29.7", {"start": v(37.11, 14.41) * mm, "mid": v(37.28, 14.8) * mm, "end": v(37.22, 15.23) * mm});
            skArc(sketch, "E13.29.8", {"start": v(35.93, 13.13) * mm, "mid": v(36.55, 13.75) * mm, "end": v(37.11, 14.41) * mm});
            skArc(sketch, "E13.29.9", {"start": v(35.66, 12.97) * mm, "mid": v(35.8, 13.04) * mm, "end": v(35.93, 13.13) * mm});
            skLineSegment(sketch, "E13.29.10", {"start": v(35.66, 12.97) * mm, "end": v(34.58, 12.58) * mm});
            skArc(sketch, "E13.29.11", {"start": v(34.58, 12.58) * mm, "mid": v(34.12, 12.17) * mm, "end": v(34.08, 11.54) * mm});
            skArc(sketch, "E13.30.0", {"start": v(29, 21.3) * mm, "mid": v(29.54, 20.97) * mm, "end": v(30.15, 21.11) * mm});
            skLineSegment(sketch, "E13.30.1", {"start": v(31.08, 21.77) * mm, "end": v(30.15, 21.11) * mm});
            skArc(sketch, "E13.30.2", {"start": v(31.37, 21.9) * mm, "mid": v(31.21, 21.85) * mm, "end": v(31.08, 21.77) * mm});
            skArc(sketch, "E13.30.3", {"start": v(31.37, 21.9) * mm, "mid": v(32.22, 22.06) * mm, "end": v(33.1, 22.13) * mm});
            skArc(sketch, "E13.30.4", {"start": v(33.82, 21.76) * mm, "mid": v(33.5, 22.04) * mm, "end": v(33.1, 22.13) * mm});
            skLineSegment(sketch, "E13.30.5", {"start": v(33.82, 21.76) * mm, "end": v(33.92, 21.6) * mm});
            skLineSegment(sketch, "E13.30.6", {"start": v(34.01, 21.46) * mm, "end": v(33.92, 21.6) * mm});
            skArc(sketch, "E13.30.7", {"start": v(34.05, 20.64) * mm, "mid": v(34.14, 21.05) * mm, "end": v(34.01, 21.46) * mm});
            skArc(sketch, "E13.30.8", {"start": v(33.1, 19.17) * mm, "mid": v(33.6, 19.88) * mm, "end": v(34.05, 20.64) * mm});
            skArc(sketch, "E13.30.9", {"start": v(32.86, 18.96) * mm, "mid": v(33, 19.06) * mm, "end": v(33.1, 19.17) * mm});
            skLineSegment(sketch, "E13.30.10", {"start": v(32.86, 18.96) * mm, "end": v(31.87, 18.4) * mm});
            skArc(sketch, "E13.30.11", {"start": v(31.87, 18.4) * mm, "mid": v(31.49, 17.9) * mm, "end": v(31.56, 17.29) * mm});
            skArc(sketch, "E13.31.0", {"start": v(24.86, 26.01) * mm, "mid": v(25.45, 25.78) * mm, "end": v(26.02, 26.03) * mm});
            skLineSegment(sketch, "E13.31.1", {"start": v(26.82, 26.83) * mm, "end": v(26.02, 26.03) * mm});
            skArc(sketch, "E13.31.2", {"start": v(27.09, 27.01) * mm, "mid": v(26.95, 26.94) * mm, "end": v(26.82, 26.83) * mm});
            skArc(sketch, "E13.31.3", {"start": v(27.09, 27.01) * mm, "mid": v(27.9, 27.32) * mm, "end": v(28.75, 27.54) * mm});
            skArc(sketch, "E13.31.4", {"start": v(29.53, 27.3) * mm, "mid": v(29.17, 27.53) * mm, "end": v(28.75, 27.54) * mm});
            skLineSegment(sketch, "E13.31.5", {"start": v(29.53, 27.3) * mm, "end": v(29.65, 27.17) * mm});
            skLineSegment(sketch, "E13.31.6", {"start": v(29.77, 27.04) * mm, "end": v(29.65, 27.17) * mm});
            skArc(sketch, "E13.31.7", {"start": v(29.94, 26.24) * mm, "mid": v(29.96, 26.66) * mm, "end": v(29.77, 27.04) * mm});
            skArc(sketch, "E13.31.8", {"start": v(29.27, 24.63) * mm, "mid": v(29.64, 25.42) * mm, "end": v(29.94, 26.24) * mm});
            skArc(sketch, "E13.31.9", {"start": v(29.07, 24.38) * mm, "mid": v(29.18, 24.5) * mm, "end": v(29.27, 24.63) * mm});
            skLineSegment(sketch, "E13.31.10", {"start": v(29.07, 24.38) * mm, "end": v(28.2, 23.65) * mm});
            skArc(sketch, "E13.31.11", {"start": v(28.2, 23.65) * mm, "mid": v(27.9, 23.1) * mm, "end": v(28.08, 22.5) * mm});
            skArc(sketch, "E13.32.0", {"start": v(19.97, 29.93) * mm, "mid": v(20.58, 29.8) * mm, "end": v(21.1, 30.15) * mm});
            skLineSegment(sketch, "E13.32.1", {"start": v(21.76, 31.08) * mm, "end": v(21.1, 30.15) * mm});
            skArc(sketch, "E13.32.2", {"start": v(21.98, 31.3) * mm, "mid": v(21.86, 31.2) * mm, "end": v(21.76, 31.08) * mm});
            skArc(sketch, "E13.32.3", {"start": v(21.98, 31.3) * mm, "mid": v(22.74, 31.75) * mm, "end": v(23.53, 32.12) * mm});
            skArc(sketch, "E13.32.4", {"start": v(24.34, 32.01) * mm, "mid": v(23.95, 32.17) * mm, "end": v(23.53, 32.12) * mm});
            skLineSegment(sketch, "E13.32.5", {"start": v(24.34, 32.01) * mm, "end": v(24.48, 31.9) * mm});
            skLineSegment(sketch, "E13.32.6", {"start": v(24.62, 31.8) * mm, "end": v(24.48, 31.9) * mm});
            skArc(sketch, "E13.32.7", {"start": v(24.93, 31.04) * mm, "mid": v(24.88, 31.46) * mm, "end": v(24.62, 31.8) * mm});
            skArc(sketch, "E13.32.8", {"start": v(24.55, 29.34) * mm, "mid": v(24.78, 30.18) * mm, "end": v(24.93, 31.04) * mm});
            skArc(sketch, "E13.32.9", {"start": v(24.4, 29.06) * mm, "mid": v(24.49, 29.2) * mm, "end": v(24.55, 29.34) * mm});
            skLineSegment(sketch, "E13.32.10", {"start": v(24.4, 29.06) * mm, "end": v(23.66, 28.2) * mm});
            skArc(sketch, "E13.32.11", {"start": v(23.66, 28.2) * mm, "mid": v(23.47, 27.6) * mm, "end": v(23.74, 27.04) * mm});
            skArc(sketch, "E13.33.0", {"start": v(14.47, 32.95) * mm, "mid": v(15.1, 32.93) * mm, "end": v(15.55, 33.36) * mm});
            skLineSegment(sketch, "E13.33.1", {"start": v(16.03, 34.4) * mm, "end": v(15.55, 33.36) * mm});
            skArc(sketch, "E13.33.2", {"start": v(16.21, 34.65) * mm, "mid": v(16.1, 34.53) * mm, "end": v(16.03, 34.4) * mm});
            skArc(sketch, "E13.33.3", {"start": v(16.21, 34.65) * mm, "mid": v(16.88, 35.21) * mm, "end": v(17.6, 35.71) * mm});
            skArc(sketch, "E13.33.4", {"start": v(18.41, 35.75) * mm, "mid": v(18, 35.84) * mm, "end": v(17.6, 35.71) * mm});
            skLineSegment(sketch, "E13.33.5", {"start": v(18.41, 35.75) * mm, "end": v(18.57, 35.67) * mm});
            skLineSegment(sketch, "E13.33.6", {"start": v(18.73, 35.59) * mm, "end": v(18.57, 35.67) * mm});
            skArc(sketch, "E13.33.7", {"start": v(19.16, 34.9) * mm, "mid": v(19.04, 35.3) * mm, "end": v(18.73, 35.59) * mm});
            skArc(sketch, "E13.33.8", {"start": v(19.08, 33.16) * mm, "mid": v(19.16, 34.02) * mm, "end": v(19.16, 34.9) * mm});
            skArc(sketch, "E13.33.9", {"start": v(18.98, 32.85) * mm, "mid": v(19.04, 33) * mm, "end": v(19.08, 33.16) * mm});
            skLineSegment(sketch, "E13.33.10", {"start": v(18.98, 32.85) * mm, "end": v(18.4, 31.87) * mm});
            skArc(sketch, "E13.33.11", {"start": v(18.4, 31.87) * mm, "mid": v(18.32, 31.25) * mm, "end": v(18.69, 30.75) * mm});
            skArc(sketch, "E13.34.0", {"start": v(8.53, 34.96) * mm, "mid": v(9.15, 35.05) * mm, "end": v(9.52, 35.55) * mm});
            skLineSegment(sketch, "E13.34.1", {"start": v(9.81, 36.65) * mm, "end": v(9.52, 35.55) * mm});
            skArc(sketch, "E13.34.2", {"start": v(9.95, 36.94) * mm, "mid": v(9.87, 36.8) * mm, "end": v(9.81, 36.65) * mm});
            skArc(sketch, "E13.34.3", {"start": v(9.95, 36.94) * mm, "mid": v(10.5, 37.6) * mm, "end": v(11.12, 38.23) * mm});
            skArc(sketch, "E13.34.4", {"start": v(11.92, 38.4) * mm, "mid": v(11.5, 38.42) * mm, "end": v(11.12, 38.23) * mm});
            skLineSegment(sketch, "E13.34.5", {"start": v(11.92, 38.4) * mm, "end": v(12.1, 38.36) * mm});
            skLineSegment(sketch, "E13.34.6", {"start": v(12.26, 38.3) * mm, "end": v(12.1, 38.36) * mm});
            skArc(sketch, "E13.34.7", {"start": v(12.81, 37.7) * mm, "mid": v(12.62, 38.07) * mm, "end": v(12.26, 38.3) * mm});
            skArc(sketch, "E13.34.8", {"start": v(13.03, 35.97) * mm, "mid": v(12.96, 36.83) * mm, "end": v(12.81, 37.7) * mm});
            skArc(sketch, "E13.34.9", {"start": v(12.98, 35.65) * mm, "mid": v(13.02, 35.8) * mm, "end": v(13.03, 35.97) * mm});
            skLineSegment(sketch, "E13.34.10", {"start": v(12.98, 35.65) * mm, "end": v(12.6, 34.58) * mm});
            skArc(sketch, "E13.34.11", {"start": v(12.6, 34.58) * mm, "mid": v(12.61, 33.96) * mm, "end": v(13.07, 33.53) * mm});
            skArc(sketch, "E13.35.0", {"start": v(2.33, 35.9) * mm, "mid": v(2.92, 36.1) * mm, "end": v(3.2, 36.66) * mm});
            skLineSegment(sketch, "E13.35.1", {"start": v(3.3, 37.8) * mm, "end": v(3.2, 36.66) * mm});
            skArc(sketch, "E13.35.2", {"start": v(3.39, 38.1) * mm, "mid": v(3.33, 37.96) * mm, "end": v(3.3, 37.8) * mm});
            skArc(sketch, "E13.35.3", {"start": v(3.39, 38.1) * mm, "mid": v(3.82, 38.86) * mm, "end": v(4.32, 39.58) * mm});
            skArc(sketch, "E13.35.4", {"start": v(5.07, 39.9) * mm, "mid": v(4.65, 39.84) * mm, "end": v(4.32, 39.58) * mm});
            skLineSegment(sketch, "E13.35.5", {"start": v(5.07, 39.9) * mm, "end": v(5.25, 39.87) * mm});
            skLineSegment(sketch, "E13.35.6", {"start": v(5.43, 39.85) * mm, "end": v(5.25, 39.87) * mm});
            skArc(sketch, "E13.35.7", {"start": v(6.07, 39.35) * mm, "mid": v(5.82, 39.68) * mm, "end": v(5.43, 39.85) * mm});
            skArc(sketch, "E13.35.8", {"start": v(6.6, 37.68) * mm, "mid": v(6.37, 38.53) * mm, "end": v(6.07, 39.35) * mm});
            skArc(sketch, "E13.35.9", {"start": v(6.6, 37.36) * mm, "mid": v(6.6, 37.52) * mm, "end": v(6.6, 37.68) * mm});
            skLineSegment(sketch, "E13.35.10", {"start": v(6.6, 37.36) * mm, "end": v(6.4, 36.24) * mm});
            skArc(sketch, "E13.35.11", {"start": v(6.4, 36.24) * mm, "mid": v(6.52, 35.63) * mm, "end": v(7.04, 35.29) * mm});
            skArc(sketch, "E14.trimOffspring", {"start": v(-15.94, 32.26) * mm, "mid": v(-16.62, 31.92) * mm, "end": v(-17.29, 31.56) * mm});
            skArc(sketch, "E15.trimOffspring", {"start": v(-10.1, 34.54) * mm, "mid": v(-10.82, 34.32) * mm, "end": v(-11.54, 34.08) * mm});
            skArc(sketch, "E16.trimOffspring", {"start": v(-29.93, 19.97) * mm, "mid": v(-30.35, 19.33) * mm, "end": v(-30.75, 18.69) * mm});
            skArc(sketch, "E17.trimOffspring", {"start": v(-32.95, 14.47) * mm, "mid": v(-33.24, 13.77) * mm, "end": v(-33.53, 13.07) * mm});
            skArc(sketch, "E18.trimOffspring", {"start": v(-34.96, 8.53) * mm, "mid": v(-35.13, 7.79) * mm, "end": v(-35.29, 7.04) * mm});
            skArc(sketch, "E19.trimOffspring", {"start": v(-35.9, 2.33) * mm, "mid": v(-35.95, 1.57) * mm, "end": v(-35.97, 0.81) * mm});
            skArc(sketch, "E20.trimOffspring", {"start": v(-35.77, -3.94) * mm, "mid": v(-35.68, -4.7) * mm, "end": v(-35.57, -5.45) * mm});
            skArc(sketch, "E21.trimOffspring", {"start": v(-34.54, -10.1) * mm, "mid": v(-34.32, -10.82) * mm, "end": v(-34.08, -11.54) * mm});
            skArc(sketch, "E22.trimOffspring", {"start": v(-32.26, -15.94) * mm, "mid": v(-31.92, -16.62) * mm, "end": v(-31.56, -17.29) * mm});
            skArc(sketch, "E23.trimOffspring", {"start": v(-29, -21.3) * mm, "mid": v(-28.55, -21.9) * mm, "end": v(-28.08, -22.5) * mm});
            skArc(sketch, "E24.trimOffspring", {"start": v(-24.86, -26.01) * mm, "mid": v(-24.3, -26.53) * mm, "end": v(-23.74, -27.04) * mm});
            skArc(sketch, "E25.trimOffspring", {"start": v(-19.97, -29.93) * mm, "mid": v(-19.33, -30.35) * mm, "end": v(-18.69, -30.75) * mm});
            skArc(sketch, "E26.trimOffspring", {"start": v(-14.47, -32.95) * mm, "mid": v(-13.77, -33.24) * mm, "end": v(-13.07, -33.53) * mm});
            skArc(sketch, "E27.trimOffspring", {"start": v(-8.53, -34.96) * mm, "mid": v(-7.79, -35.13) * mm, "end": v(-7.04, -35.29) * mm});
            skArc(sketch, "E28.trimOffspring", {"start": v(-2.33, -35.9) * mm, "mid": v(-1.57, -35.95) * mm, "end": v(-0.81, -35.97) * mm});
            skArc(sketch, "E29.trimOffspring", {"start": v(3.94, -35.77) * mm, "mid": v(4.7, -35.68) * mm, "end": v(5.45, -35.57) * mm});
            skArc(sketch, "E30.trimOffspring", {"start": v(10.1, -34.54) * mm, "mid": v(10.82, -34.32) * mm, "end": v(11.54, -34.08) * mm});
            skArc(sketch, "E31.trimOffspring", {"start": v(15.94, -32.26) * mm, "mid": v(16.62, -31.92) * mm, "end": v(17.29, -31.56) * mm});
            skArc(sketch, "E32.trimOffspring", {"start": v(21.3, -29) * mm, "mid": v(21.9, -28.55) * mm, "end": v(22.5, -28.08) * mm});
            skArc(sketch, "E33.trimOffspring", {"start": v(26.01, -24.86) * mm, "mid": v(26.53, -24.3) * mm, "end": v(27.04, -23.74) * mm});
            skArc(sketch, "E34.trimOffspring", {"start": v(29.93, -19.97) * mm, "mid": v(30.35, -19.33) * mm, "end": v(30.75, -18.69) * mm});
            skArc(sketch, "E35.trimOffspring", {"start": v(32.95, -14.47) * mm, "mid": v(33.24, -13.77) * mm, "end": v(33.53, -13.07) * mm});
            skArc(sketch, "E36.trimOffspring", {"start": v(34.96, -8.53) * mm, "mid": v(35.13, -7.79) * mm, "end": v(35.29, -7.04) * mm});
            skArc(sketch, "E37.trimOffspring", {"start": v(35.9, -2.33) * mm, "mid": v(35.95, -1.57) * mm, "end": v(35.97, -0.81) * mm});
            skArc(sketch, "E38.trimOffspring", {"start": v(35.77, 3.94) * mm, "mid": v(35.68, 4.7) * mm, "end": v(35.57, 5.45) * mm});
            skArc(sketch, "E39.trimOffspring", {"start": v(34.54, 10.1) * mm, "mid": v(34.32, 10.82) * mm, "end": v(34.08, 11.54) * mm});
            skArc(sketch, "E40.trimOffspring", {"start": v(32.26, 15.94) * mm, "mid": v(31.92, 16.62) * mm, "end": v(31.56, 17.29) * mm});
            skArc(sketch, "E41.trimOffspring", {"start": v(29, 21.3) * mm, "mid": v(28.55, 21.9) * mm, "end": v(28.08, 22.5) * mm});
            skArc(sketch, "E42.trimOffspring", {"start": v(24.86, 26.01) * mm, "mid": v(24.3, 26.53) * mm, "end": v(23.74, 27.04) * mm});
            skArc(sketch, "E43.trimOffspring", {"start": v(19.97, 29.93) * mm, "mid": v(19.33, 30.35) * mm, "end": v(18.69, 30.75) * mm});
            skArc(sketch, "E44.trimOffspring", {"start": v(14.47, 32.95) * mm, "mid": v(13.77, 33.24) * mm, "end": v(13.07, 33.53) * mm});
            skArc(sketch, "E45.trimOffspring", {"start": v(8.53, 34.96) * mm, "mid": v(7.79, 35.13) * mm, "end": v(7.04, 35.29) * mm});
            skArc(sketch, "E46.trimOffspring", {"start": v(2.33, 35.9) * mm, "mid": v(1.57, 35.95) * mm, "end": v(0.81, 35.97) * mm});
            skArc(sketch, "E47.trimOffspring", {"start": v(-21.3, 29) * mm, "mid": v(-21.9, 28.55) * mm, "end": v(-22.5, 28.08) * mm});
            skArc(sketch, "E48.trimOffspring", {"start": v(-26.01, 24.86) * mm, "mid": v(-26.53, 24.3) * mm, "end": v(-27.04, 23.74) * mm});
            skSolve(sketch);
        }
        {
            var Q0;
            Q0=makeQuery(id+"F0.imprint","IMPRINT",FACE,{"disambiguationData":[TD([[makeQuery(id+"F0.imprint","IMPRINT",EDGE,{"derivedFrom":sQuery(id+"F0.wireOp",EDGE,"E0")}),1.0]])]});
            extrude(context, id + "F1", {"entities" : qUnion([Q0]), "depth" : 12.7 * mm});
        }
        {
            var Q0;
            Q0=makeQuery(id+"F1.opExtrude","CAP_FACE",FACE,{"disambiguationData":[OSD([sQuery(id+"F0.wireOp",EDGE,"E0"),sQuery(id+"F0.wireOp",EDGE,"E1"),sQuery(id+"F0.wireOp",EDGE,"E2"),sQuery(id+"F0.wireOp",EDGE,"E3"),sQuery(id+"F0.wireOp",EDGE,"E4.MirrorCS"),sQuery(id+"F0.wireOp",EDGE,"E5.MirrorCS"),sQuery(id+"F0.wireOp",EDGE,"E6.MirrorCS"),sQuery(id+"F0.wireOp",EDGE,"E7.filletArc"),sQuery(id+"F0.wireOp",EDGE,"E8.filletArc"),sQuery(id+"F0.wireOp",EDGE,"E9.filletArc"),sQuery(id+"F0.wireOp",EDGE,"E10.filletArc"),sQuery(id+"F0.wireOp",EDGE,"E11.filletArc"),sQuery(id+"F0.wireOp",EDGE,"E12.filletArc"),sQuery(id+"F0.wireOp",EDGE,"E13.1.0"),sQuery(id+"F0.wireOp",EDGE,"E13.1.1"),sQuery(id+"F0.wireOp",EDGE,"E13.1.2"),sQuery(id+"F0.wireOp",EDGE,"E13.1.3"),sQuery(id+"F0.wireOp",EDGE,"E13.1.4"),sQuery(id+"F0.wireOp",EDGE,"E13.1.5"),sQuery(id+"F0.wireOp",EDGE,"E13.1.6"),sQuery(id+"F0.wireOp",EDGE,"E13.1.7"),sQuery(id+"F0.wireOp",EDGE,"E13.1.8"),sQuery(id+"F0.wireOp",EDGE,"E13.1.9"),sQuery(id+"F0.wireOp",EDGE,"E13.1.10"),sQuery(id+"F0.wireOp",EDGE,"E13.1.11"),sQuery(id+"F0.wireOp",EDGE,"E13.2.0"),sQuery(id+"F0.wireOp",EDGE,"E13.2.1"),sQuery(id+"F0.wireOp",EDGE,"E13.2.2"),sQuery(id+"F0.wireOp",EDGE,"E13.2.3"),sQuery(id+"F0.wireOp",EDGE,"E13.2.4"),sQuery(id+"F0.wireOp",EDGE,"E13.2.5"),sQuery(id+"F0.wireOp",EDGE,"E13.2.6"),sQuery(id+"F0.wireOp",EDGE,"E13.2.7"),sQuery(id+"F0.wireOp",EDGE,"E13.2.8"),sQuery(id+"F0.wireOp",EDGE,"E13.2.9"),sQuery(id+"F0.wireOp",EDGE,"E13.2.10"),sQuery(id+"F0.wireOp",EDGE,"E13.2.11"),sQuery(id+"F0.wireOp",EDGE,"E13.3.0"),sQuery(id+"F0.wireOp",EDGE,"E13.3.1"),sQuery(id+"F0.wireOp",EDGE,"E13.3.2"),sQuery(id+"F0.wireOp",EDGE,"E13.3.3"),sQuery(id+"F0.wireOp",EDGE,"E13.3.4"),sQuery(id+"F0.wireOp",EDGE,"E13.3.5"),sQuery(id+"F0.wireOp",EDGE,"E13.3.6"),sQuery(id+"F0.wireOp",EDGE,"E13.3.7"),sQuery(id+"F0.wireOp",EDGE,"E13.3.8"),sQuery(id+"F0.wireOp",EDGE,"E13.3.9"),sQuery(id+"F0.wireOp",EDGE,"E13.3.10"),sQuery(id+"F0.wireOp",EDGE,"E13.3.11"),sQuery(id+"F0.wireOp",EDGE,"E13.4.0"),sQuery(id+"F0.wireOp",EDGE,"E13.4.1"),sQuery(id+"F0.wireOp",EDGE,"E13.4.2"),sQuery(id+"F0.wireOp",EDGE,"E13.4.3"),sQuery(id+"F0.wireOp",EDGE,"E13.4.4"),sQuery(id+"F0.wireOp",EDGE,"E13.4.5"),sQuery(id+"F0.wireOp",EDGE,"E13.4.6"),sQuery(id+"F0.wireOp",EDGE,"E13.4.7"),sQuery(id+"F0.wireOp",EDGE,"E13.4.8"),sQuery(id+"F0.wireOp",EDGE,"E13.4.9"),sQuery(id+"F0.wireOp",EDGE,"E13.4.10"),sQuery(id+"F0.wireOp",EDGE,"E13.4.11"),sQuery(id+"F0.wireOp",EDGE,"E13.5.0"),sQuery(id+"F0.wireOp",EDGE,"E13.5.1"),sQuery(id+"F0.wireOp",EDGE,"E13.5.2"),sQuery(id+"F0.wireOp",EDGE,"E13.5.3"),sQuery(id+"F0.wireOp",EDGE,"E13.5.4"),sQuery(id+"F0.wireOp",EDGE,"E13.5.5"),sQuery(id+"F0.wireOp",EDGE,"E13.5.6"),sQuery(id+"F0.wireOp",EDGE,"E13.5.7"),sQuery(id+"F0.wireOp",EDGE,"E13.5.8"),sQuery(id+"F0.wireOp",EDGE,"E13.5.9"),sQuery(id+"F0.wireOp",EDGE,"E13.5.10"),sQuery(id+"F0.wireOp",EDGE,"E13.5.11"),sQuery(id+"F0.wireOp",EDGE,"E13.6.0"),sQuery(id+"F0.wireOp",EDGE,"E13.6.1"),sQuery(id+"F0.wireOp",EDGE,"E13.6.2"),sQuery(id+"F0.wireOp",EDGE,"E13.6.3"),sQuery(id+"F0.wireOp",EDGE,"E13.6.4"),sQuery(id+"F0.wireOp",EDGE,"E13.6.5"),sQuery(id+"F0.wireOp",EDGE,"E13.6.6"),sQuery(id+"F0.wireOp",EDGE,"E13.6.7"),sQuery(id+"F0.wireOp",EDGE,"E13.6.8"),sQuery(id+"F0.wireOp",EDGE,"E13.6.9"),sQuery(id+"F0.wireOp",EDGE,"E13.6.10"),sQuery(id+"F0.wireOp",EDGE,"E13.6.11"),sQuery(id+"F0.wireOp",EDGE,"E13.7.0"),sQuery(id+"F0.wireOp",EDGE,"E13.7.1"),sQuery(id+"F0.wireOp",EDGE,"E13.7.2"),sQuery(id+"F0.wireOp",EDGE,"E13.7.3"),sQuery(id+"F0.wireOp",EDGE,"E13.7.4"),sQuery(id+"F0.wireOp",EDGE,"E13.7.5"),sQuery(id+"F0.wireOp",EDGE,"E13.7.6"),sQuery(id+"F0.wireOp",EDGE,"E13.7.7"),sQuery(id+"F0.wireOp",EDGE,"E13.7.8"),sQuery(id+"F0.wireOp",EDGE,"E13.7.9"),sQuery(id+"F0.wireOp",EDGE,"E13.7.10"),sQuery(id+"F0.wireOp",EDGE,"E13.7.11"),sQuery(id+"F0.wireOp",EDGE,"E13.8.0"),sQuery(id+"F0.wireOp",EDGE,"E13.8.1"),sQuery(id+"F0.wireOp",EDGE,"E13.8.2"),sQuery(id+"F0.wireOp",EDGE,"E13.8.3"),sQuery(id+"F0.wireOp",EDGE,"E13.8.4"),sQuery(id+"F0.wireOp",EDGE,"E13.8.5"),sQuery(id+"F0.wireOp",EDGE,"E13.8.6"),sQuery(id+"F0.wireOp",EDGE,"E13.8.7"),sQuery(id+"F0.wireOp",EDGE,"E13.8.8"),sQuery(id+"F0.wireOp",EDGE,"E13.8.9"),sQuery(id+"F0.wireOp",EDGE,"E13.8.10"),sQuery(id+"F0.wireOp",EDGE,"E13.8.11"),sQuery(id+"F0.wireOp",EDGE,"E13.9.0"),sQuery(id+"F0.wireOp",EDGE,"E13.9.1"),sQuery(id+"F0.wireOp",EDGE,"E13.9.2"),sQuery(id+"F0.wireOp",EDGE,"E13.9.3"),sQuery(id+"F0.wireOp",EDGE,"E13.9.4"),sQuery(id+"F0.wireOp",EDGE,"E13.9.5"),sQuery(id+"F0.wireOp",EDGE,"E13.9.6"),sQuery(id+"F0.wireOp",EDGE,"E13.9.7"),sQuery(id+"F0.wireOp",EDGE,"E13.9.8"),sQuery(id+"F0.wireOp",EDGE,"E13.9.9"),sQuery(id+"F0.wireOp",EDGE,"E13.9.10"),sQuery(id+"F0.wireOp",EDGE,"E13.9.11"),sQuery(id+"F0.wireOp",EDGE,"E13.10.0"),sQuery(id+"F0.wireOp",EDGE,"E13.10.1"),sQuery(id+"F0.wireOp",EDGE,"E13.10.2"),sQuery(id+"F0.wireOp",EDGE,"E13.10.3"),sQuery(id+"F0.wireOp",EDGE,"E13.10.4"),sQuery(id+"F0.wireOp",EDGE,"E13.10.5"),sQuery(id+"F0.wireOp",EDGE,"E13.10.6"),sQuery(id+"F0.wireOp",EDGE,"E13.10.7"),sQuery(id+"F0.wireOp",EDGE,"E13.10.8"),sQuery(id+"F0.wireOp",EDGE,"E13.10.9"),sQuery(id+"F0.wireOp",EDGE,"E13.10.10"),sQuery(id+"F0.wireOp",EDGE,"E13.10.11"),sQuery(id+"F0.wireOp",EDGE,"E13.11.0"),sQuery(id+"F0.wireOp",EDGE,"E13.11.1"),sQuery(id+"F0.wireOp",EDGE,"E13.11.2"),sQuery(id+"F0.wireOp",EDGE,"E13.11.3"),sQuery(id+"F0.wireOp",EDGE,"E13.11.4"),sQuery(id+"F0.wireOp",EDGE,"E13.11.5"),sQuery(id+"F0.wireOp",EDGE,"E13.11.6"),sQuery(id+"F0.wireOp",EDGE,"E13.11.7"),sQuery(id+"F0.wireOp",EDGE,"E13.11.8"),sQuery(id+"F0.wireOp",EDGE,"E13.11.9"),sQuery(id+"F0.wireOp",EDGE,"E13.11.10"),sQuery(id+"F0.wireOp",EDGE,"E13.11.11"),sQuery(id+"F0.wireOp",EDGE,"E13.12.0"),sQuery(id+"F0.wireOp",EDGE,"E13.12.1"),sQuery(id+"F0.wireOp",EDGE,"E13.12.2"),sQuery(id+"F0.wireOp",EDGE,"E13.12.3"),sQuery(id+"F0.wireOp",EDGE,"E13.12.4"),sQuery(id+"F0.wireOp",EDGE,"E13.12.5"),sQuery(id+"F0.wireOp",EDGE,"E13.12.6"),sQuery(id+"F0.wireOp",EDGE,"E13.12.7"),sQuery(id+"F0.wireOp",EDGE,"E13.12.8"),sQuery(id+"F0.wireOp",EDGE,"E13.12.9"),sQuery(id+"F0.wireOp",EDGE,"E13.12.10"),sQuery(id+"F0.wireOp",EDGE,"E13.12.11"),sQuery(id+"F0.wireOp",EDGE,"E13.13.0"),sQuery(id+"F0.wireOp",EDGE,"E13.13.1"),sQuery(id+"F0.wireOp",EDGE,"E13.13.2"),sQuery(id+"F0.wireOp",EDGE,"E13.13.3"),sQuery(id+"F0.wireOp",EDGE,"E13.13.4"),sQuery(id+"F0.wireOp",EDGE,"E13.13.5"),sQuery(id+"F0.wireOp",EDGE,"E13.13.6"),sQuery(id+"F0.wireOp",EDGE,"E13.13.7"),sQuery(id+"F0.wireOp",EDGE,"E13.13.8"),sQuery(id+"F0.wireOp",EDGE,"E13.13.9"),sQuery(id+"F0.wireOp",EDGE,"E13.13.10"),sQuery(id+"F0.wireOp",EDGE,"E13.13.11"),sQuery(id+"F0.wireOp",EDGE,"E13.14.0"),sQuery(id+"F0.wireOp",EDGE,"E13.14.1"),sQuery(id+"F0.wireOp",EDGE,"E13.14.2"),sQuery(id+"F0.wireOp",EDGE,"E13.14.3"),sQuery(id+"F0.wireOp",EDGE,"E13.14.4"),sQuery(id+"F0.wireOp",EDGE,"E13.14.5"),sQuery(id+"F0.wireOp",EDGE,"E13.14.6"),sQuery(id+"F0.wireOp",EDGE,"E13.14.7"),sQuery(id+"F0.wireOp",EDGE,"E13.14.8"),sQuery(id+"F0.wireOp",EDGE,"E13.14.9"),sQuery(id+"F0.wireOp",EDGE,"E13.14.10"),sQuery(id+"F0.wireOp",EDGE,"E13.14.11"),sQuery(id+"F0.wireOp",EDGE,"E13.15.0"),sQuery(id+"F0.wireOp",EDGE,"E13.15.1"),sQuery(id+"F0.wireOp",EDGE,"E13.15.2"),sQuery(id+"F0.wireOp",EDGE,"E13.15.3"),sQuery(id+"F0.wireOp",EDGE,"E13.15.4"),sQuery(id+"F0.wireOp",EDGE,"E13.15.5"),sQuery(id+"F0.wireOp",EDGE,"E13.15.6"),sQuery(id+"F0.wireOp",EDGE,"E13.15.7"),sQuery(id+"F0.wireOp",EDGE,"E13.15.8"),sQuery(id+"F0.wireOp",EDGE,"E13.15.9"),sQuery(id+"F0.wireOp",EDGE,"E13.15.10"),sQuery(id+"F0.wireOp",EDGE,"E13.15.11"),sQuery(id+"F0.wireOp",EDGE,"E13.16.0"),sQuery(id+"F0.wireOp",EDGE,"E13.16.1"),sQuery(id+"F0.wireOp",EDGE,"E13.16.2"),sQuery(id+"F0.wireOp",EDGE,"E13.16.3"),sQuery(id+"F0.wireOp",EDGE,"E13.16.4"),sQuery(id+"F0.wireOp",EDGE,"E13.16.5"),sQuery(id+"F0.wireOp",EDGE,"E13.16.6"),sQuery(id+"F0.wireOp",EDGE,"E13.16.7"),sQuery(id+"F0.wireOp",EDGE,"E13.16.8"),sQuery(id+"F0.wireOp",EDGE,"E13.16.9"),sQuery(id+"F0.wireOp",EDGE,"E13.16.10"),sQuery(id+"F0.wireOp",EDGE,"E13.16.11"),sQuery(id+"F0.wireOp",EDGE,"E13.17.0"),sQuery(id+"F0.wireOp",EDGE,"E13.17.1"),sQuery(id+"F0.wireOp",EDGE,"E13.17.2"),sQuery(id+"F0.wireOp",EDGE,"E13.17.3"),sQuery(id+"F0.wireOp",EDGE,"E13.17.4"),sQuery(id+"F0.wireOp",EDGE,"E13.17.5"),sQuery(id+"F0.wireOp",EDGE,"E13.17.6"),sQuery(id+"F0.wireOp",EDGE,"E13.17.7"),sQuery(id+"F0.wireOp",EDGE,"E13.17.8"),sQuery(id+"F0.wireOp",EDGE,"E13.17.9"),sQuery(id+"F0.wireOp",EDGE,"E13.17.10"),sQuery(id+"F0.wireOp",EDGE,"E13.17.11"),sQuery(id+"F0.wireOp",EDGE,"E13.18.0"),sQuery(id+"F0.wireOp",EDGE,"E13.18.1"),sQuery(id+"F0.wireOp",EDGE,"E13.18.2"),sQuery(id+"F0.wireOp",EDGE,"E13.18.3"),sQuery(id+"F0.wireOp",EDGE,"E13.18.4"),sQuery(id+"F0.wireOp",EDGE,"E13.18.5"),sQuery(id+"F0.wireOp",EDGE,"E13.18.6"),sQuery(id+"F0.wireOp",EDGE,"E13.18.7"),sQuery(id+"F0.wireOp",EDGE,"E13.18.8"),sQuery(id+"F0.wireOp",EDGE,"E13.18.9"),sQuery(id+"F0.wireOp",EDGE,"E13.18.10"),sQuery(id+"F0.wireOp",EDGE,"E13.18.11"),sQuery(id+"F0.wireOp",EDGE,"E13.19.0"),sQuery(id+"F0.wireOp",EDGE,"E13.19.1"),sQuery(id+"F0.wireOp",EDGE,"E13.19.2"),sQuery(id+"F0.wireOp",EDGE,"E13.19.3"),sQuery(id+"F0.wireOp",EDGE,"E13.19.4"),sQuery(id+"F0.wireOp",EDGE,"E13.19.5"),sQuery(id+"F0.wireOp",EDGE,"E13.19.6"),sQuery(id+"F0.wireOp",EDGE,"E13.19.7"),sQuery(id+"F0.wireOp",EDGE,"E13.19.8"),sQuery(id+"F0.wireOp",EDGE,"E13.19.9"),sQuery(id+"F0.wireOp",EDGE,"E13.19.10"),sQuery(id+"F0.wireOp",EDGE,"E13.19.11"),sQuery(id+"F0.wireOp",EDGE,"E13.20.0"),sQuery(id+"F0.wireOp",EDGE,"E13.20.1"),sQuery(id+"F0.wireOp",EDGE,"E13.20.2"),sQuery(id+"F0.wireOp",EDGE,"E13.20.3"),sQuery(id+"F0.wireOp",EDGE,"E13.20.4"),sQuery(id+"F0.wireOp",EDGE,"E13.20.5"),sQuery(id+"F0.wireOp",EDGE,"E13.20.6"),sQuery(id+"F0.wireOp",EDGE,"E13.20.7"),sQuery(id+"F0.wireOp",EDGE,"E13.20.8"),sQuery(id+"F0.wireOp",EDGE,"E13.20.9"),sQuery(id+"F0.wireOp",EDGE,"E13.20.10"),sQuery(id+"F0.wireOp",EDGE,"E13.20.11"),sQuery(id+"F0.wireOp",EDGE,"E13.21.0"),sQuery(id+"F0.wireOp",EDGE,"E13.21.1"),sQuery(id+"F0.wireOp",EDGE,"E13.21.2"),sQuery(id+"F0.wireOp",EDGE,"E13.21.3"),sQuery(id+"F0.wireOp",EDGE,"E13.21.4"),sQuery(id+"F0.wireOp",EDGE,"E13.21.5"),sQuery(id+"F0.wireOp",EDGE,"E13.21.6"),sQuery(id+"F0.wireOp",EDGE,"E13.21.7"),sQuery(id+"F0.wireOp",EDGE,"E13.21.8"),sQuery(id+"F0.wireOp",EDGE,"E13.21.9"),sQuery(id+"F0.wireOp",EDGE,"E13.21.10"),sQuery(id+"F0.wireOp",EDGE,"E13.21.11"),sQuery(id+"F0.wireOp",EDGE,"E13.22.0"),sQuery(id+"F0.wireOp",EDGE,"E13.22.1"),sQuery(id+"F0.wireOp",EDGE,"E13.22.2"),sQuery(id+"F0.wireOp",EDGE,"E13.22.3"),sQuery(id+"F0.wireOp",EDGE,"E13.22.4"),sQuery(id+"F0.wireOp",EDGE,"E13.22.5"),sQuery(id+"F0.wireOp",EDGE,"E13.22.6"),sQuery(id+"F0.wireOp",EDGE,"E13.22.7"),sQuery(id+"F0.wireOp",EDGE,"E13.22.8"),sQuery(id+"F0.wireOp",EDGE,"E13.22.9"),sQuery(id+"F0.wireOp",EDGE,"E13.22.10"),sQuery(id+"F0.wireOp",EDGE,"E13.22.11"),sQuery(id+"F0.wireOp",EDGE,"E13.23.0"),sQuery(id+"F0.wireOp",EDGE,"E13.23.1"),sQuery(id+"F0.wireOp",EDGE,"E13.23.2"),sQuery(id+"F0.wireOp",EDGE,"E13.23.3"),sQuery(id+"F0.wireOp",EDGE,"E13.23.4"),sQuery(id+"F0.wireOp",EDGE,"E13.23.5"),sQuery(id+"F0.wireOp",EDGE,"E13.23.6"),sQuery(id+"F0.wireOp",EDGE,"E13.23.7"),sQuery(id+"F0.wireOp",EDGE,"E13.23.8"),sQuery(id+"F0.wireOp",EDGE,"E13.23.9"),sQuery(id+"F0.wireOp",EDGE,"E13.23.10"),sQuery(id+"F0.wireOp",EDGE,"E13.23.11"),sQuery(id+"F0.wireOp",EDGE,"E13.24.0"),sQuery(id+"F0.wireOp",EDGE,"E13.24.1"),sQuery(id+"F0.wireOp",EDGE,"E13.24.2"),sQuery(id+"F0.wireOp",EDGE,"E13.24.3"),sQuery(id+"F0.wireOp",EDGE,"E13.24.4"),sQuery(id+"F0.wireOp",EDGE,"E13.24.5"),sQuery(id+"F0.wireOp",EDGE,"E13.24.6"),sQuery(id+"F0.wireOp",EDGE,"E13.24.7"),sQuery(id+"F0.wireOp",EDGE,"E13.24.8"),sQuery(id+"F0.wireOp",EDGE,"E13.24.9"),sQuery(id+"F0.wireOp",EDGE,"E13.24.10"),sQuery(id+"F0.wireOp",EDGE,"E13.24.11"),sQuery(id+"F0.wireOp",EDGE,"E13.25.0"),sQuery(id+"F0.wireOp",EDGE,"E13.25.1"),sQuery(id+"F0.wireOp",EDGE,"E13.25.2"),sQuery(id+"F0.wireOp",EDGE,"E13.25.3"),sQuery(id+"F0.wireOp",EDGE,"E13.25.4"),sQuery(id+"F0.wireOp",EDGE,"E13.25.5"),sQuery(id+"F0.wireOp",EDGE,"E13.25.6"),sQuery(id+"F0.wireOp",EDGE,"E13.25.7"),sQuery(id+"F0.wireOp",EDGE,"E13.25.8"),sQuery(id+"F0.wireOp",EDGE,"E13.25.9"),sQuery(id+"F0.wireOp",EDGE,"E13.25.10"),sQuery(id+"F0.wireOp",EDGE,"E13.25.11"),sQuery(id+"F0.wireOp",EDGE,"E13.26.0"),sQuery(id+"F0.wireOp",EDGE,"E13.26.1"),sQuery(id+"F0.wireOp",EDGE,"E13.26.2"),sQuery(id+"F0.wireOp",EDGE,"E13.26.3"),sQuery(id+"F0.wireOp",EDGE,"E13.26.4"),sQuery(id+"F0.wireOp",EDGE,"E13.26.5"),sQuery(id+"F0.wireOp",EDGE,"E13.26.6"),sQuery(id+"F0.wireOp",EDGE,"E13.26.7"),sQuery(id+"F0.wireOp",EDGE,"E13.26.8"),sQuery(id+"F0.wireOp",EDGE,"E13.26.9"),sQuery(id+"F0.wireOp",EDGE,"E13.26.10"),sQuery(id+"F0.wireOp",EDGE,"E13.26.11"),sQuery(id+"F0.wireOp",EDGE,"E13.27.0"),sQuery(id+"F0.wireOp",EDGE,"E13.27.1"),sQuery(id+"F0.wireOp",EDGE,"E13.27.2"),sQuery(id+"F0.wireOp",EDGE,"E13.27.3"),sQuery(id+"F0.wireOp",EDGE,"E13.27.4"),sQuery(id+"F0.wireOp",EDGE,"E13.27.5"),sQuery(id+"F0.wireOp",EDGE,"E13.27.6"),sQuery(id+"F0.wireOp",EDGE,"E13.27.7"),sQuery(id+"F0.wireOp",EDGE,"E13.27.8"),sQuery(id+"F0.wireOp",EDGE,"E13.27.9"),sQuery(id+"F0.wireOp",EDGE,"E13.27.10"),sQuery(id+"F0.wireOp",EDGE,"E13.27.11"),sQuery(id+"F0.wireOp",EDGE,"E13.28.0"),sQuery(id+"F0.wireOp",EDGE,"E13.28.1"),sQuery(id+"F0.wireOp",EDGE,"E13.28.2"),sQuery(id+"F0.wireOp",EDGE,"E13.28.3"),sQuery(id+"F0.wireOp",EDGE,"E13.28.4"),sQuery(id+"F0.wireOp",EDGE,"E13.28.5"),sQuery(id+"F0.wireOp",EDGE,"E13.28.6"),sQuery(id+"F0.wireOp",EDGE,"E13.28.7"),sQuery(id+"F0.wireOp",EDGE,"E13.28.8"),sQuery(id+"F0.wireOp",EDGE,"E13.28.9"),sQuery(id+"F0.wireOp",EDGE,"E13.28.10"),sQuery(id+"F0.wireOp",EDGE,"E13.28.11"),sQuery(id+"F0.wireOp",EDGE,"E13.29.0"),sQuery(id+"F0.wireOp",EDGE,"E13.29.1"),sQuery(id+"F0.wireOp",EDGE,"E13.29.2"),sQuery(id+"F0.wireOp",EDGE,"E13.29.3"),sQuery(id+"F0.wireOp",EDGE,"E13.29.4"),sQuery(id+"F0.wireOp",EDGE,"E13.29.5"),sQuery(id+"F0.wireOp",EDGE,"E13.29.6"),sQuery(id+"F0.wireOp",EDGE,"E13.29.7"),sQuery(id+"F0.wireOp",EDGE,"E13.29.8"),sQuery(id+"F0.wireOp",EDGE,"E13.29.9"),sQuery(id+"F0.wireOp",EDGE,"E13.29.10"),sQuery(id+"F0.wireOp",EDGE,"E13.29.11"),sQuery(id+"F0.wireOp",EDGE,"E13.30.0"),sQuery(id+"F0.wireOp",EDGE,"E13.30.1"),sQuery(id+"F0.wireOp",EDGE,"E13.30.2"),sQuery(id+"F0.wireOp",EDGE,"E13.30.3"),sQuery(id+"F0.wireOp",EDGE,"E13.30.4"),sQuery(id+"F0.wireOp",EDGE,"E13.30.5"),sQuery(id+"F0.wireOp",EDGE,"E13.30.6"),sQuery(id+"F0.wireOp",EDGE,"E13.30.7"),sQuery(id+"F0.wireOp",EDGE,"E13.30.8"),sQuery(id+"F0.wireOp",EDGE,"E13.30.9"),sQuery(id+"F0.wireOp",EDGE,"E13.30.10"),sQuery(id+"F0.wireOp",EDGE,"E13.30.11"),sQuery(id+"F0.wireOp",EDGE,"E13.31.0"),sQuery(id+"F0.wireOp",EDGE,"E13.31.1"),sQuery(id+"F0.wireOp",EDGE,"E13.31.2"),sQuery(id+"F0.wireOp",EDGE,"E13.31.3"),sQuery(id+"F0.wireOp",EDGE,"E13.31.4"),sQuery(id+"F0.wireOp",EDGE,"E13.31.5"),sQuery(id+"F0.wireOp",EDGE,"E13.31.6"),sQuery(id+"F0.wireOp",EDGE,"E13.31.7"),sQuery(id+"F0.wireOp",EDGE,"E13.31.8"),sQuery(id+"F0.wireOp",EDGE,"E13.31.9"),sQuery(id+"F0.wireOp",EDGE,"E13.31.10"),sQuery(id+"F0.wireOp",EDGE,"E13.31.11"),sQuery(id+"F0.wireOp",EDGE,"E13.32.0"),sQuery(id+"F0.wireOp",EDGE,"E13.32.1"),sQuery(id+"F0.wireOp",EDGE,"E13.32.2"),sQuery(id+"F0.wireOp",EDGE,"E13.32.3"),sQuery(id+"F0.wireOp",EDGE,"E13.32.4"),sQuery(id+"F0.wireOp",EDGE,"E13.32.5"),sQuery(id+"F0.wireOp",EDGE,"E13.32.6"),sQuery(id+"F0.wireOp",EDGE,"E13.32.7"),sQuery(id+"F0.wireOp",EDGE,"E13.32.8"),sQuery(id+"F0.wireOp",EDGE,"E13.32.9"),sQuery(id+"F0.wireOp",EDGE,"E13.32.10"),sQuery(id+"F0.wireOp",EDGE,"E13.32.11"),sQuery(id+"F0.wireOp",EDGE,"E13.33.0"),sQuery(id+"F0.wireOp",EDGE,"E13.33.1"),sQuery(id+"F0.wireOp",EDGE,"E13.33.2"),sQuery(id+"F0.wireOp",EDGE,"E13.33.3"),sQuery(id+"F0.wireOp",EDGE,"E13.33.4"),sQuery(id+"F0.wireOp",EDGE,"E13.33.5"),sQuery(id+"F0.wireOp",EDGE,"E13.33.6"),sQuery(id+"F0.wireOp",EDGE,"E13.33.7"),sQuery(id+"F0.wireOp",EDGE,"E13.33.8"),sQuery(id+"F0.wireOp",EDGE,"E13.33.9"),sQuery(id+"F0.wireOp",EDGE,"E13.33.10"),sQuery(id+"F0.wireOp",EDGE,"E13.33.11"),sQuery(id+"F0.wireOp",EDGE,"E13.34.0"),sQuery(id+"F0.wireOp",EDGE,"E13.34.1"),sQuery(id+"F0.wireOp",EDGE,"E13.34.2"),sQuery(id+"F0.wireOp",EDGE,"E13.34.3"),sQuery(id+"F0.wireOp",EDGE,"E13.34.4"),sQuery(id+"F0.wireOp",EDGE,"E13.34.5"),sQuery(id+"F0.wireOp",EDGE,"E13.34.6"),sQuery(id+"F0.wireOp",EDGE,"E13.34.7"),sQuery(id+"F0.wireOp",EDGE,"E13.34.8"),sQuery(id+"F0.wireOp",EDGE,"E13.34.9"),sQuery(id+"F0.wireOp",EDGE,"E13.34.10"),sQuery(id+"F0.wireOp",EDGE,"E13.34.11"),sQuery(id+"F0.wireOp",EDGE,"E13.35.0"),sQuery(id+"F0.wireOp",EDGE,"E13.35.1"),sQuery(id+"F0.wireOp",EDGE,"E13.35.2"),sQuery(id+"F0.wireOp",EDGE,"E13.35.3"),sQuery(id+"F0.wireOp",EDGE,"E13.35.4"),sQuery(id+"F0.wireOp",EDGE,"E13.35.5"),sQuery(id+"F0.wireOp",EDGE,"E13.35.6"),sQuery(id+"F0.wireOp",EDGE,"E13.35.7"),sQuery(id+"F0.wireOp",EDGE,"E13.35.8"),sQuery(id+"F0.wireOp",EDGE,"E13.35.9"),sQuery(id+"F0.wireOp",EDGE,"E13.35.10"),sQuery(id+"F0.wireOp",EDGE,"E13.35.11"),sQuery(id+"F0.wireOp",EDGE,"E14.trimOffspring"),sQuery(id+"F0.wireOp",EDGE,"E15.trimOffspring"),sQuery(id+"F0.wireOp",EDGE,"E16.trimOffspring"),sQuery(id+"F0.wireOp",EDGE,"E17.trimOffspring"),sQuery(id+"F0.wireOp",EDGE,"E18.trimOffspring"),sQuery(id+"F0.wireOp",EDGE,"E19.trimOffspring"),sQuery(id+"F0.wireOp",EDGE,"E20.trimOffspring"),sQuery(id+"F0.wireOp",EDGE,"E21.trimOffspring"),sQuery(id+"F0.wireOp",EDGE,"E22.trimOffspring"),sQuery(id+"F0.wireOp",EDGE,"E23.trimOffspring"),sQuery(id+"F0.wireOp",EDGE,"E24.trimOffspring"),sQuery(id+"F0.wireOp",EDGE,"E25.trimOffspring"),sQuery(id+"F0.wireOp",EDGE,"E26.trimOffspring"),sQuery(id+"F0.wireOp",EDGE,"E27.trimOffspring"),sQuery(id+"F0.wireOp",EDGE,"E28.trimOffspring"),sQuery(id+"F0.wireOp",EDGE,"E29.trimOffspring"),sQuery(id+"F0.wireOp",EDGE,"E30.trimOffspring"),sQuery(id+"F0.wireOp",EDGE,"E31.trimOffspring"),sQuery(id+"F0.wireOp",EDGE,"E32.trimOffspring"),sQuery(id+"F0.wireOp",EDGE,"E33.trimOffspring"),sQuery(id+"F0.wireOp",EDGE,"E34.trimOffspring"),sQuery(id+"F0.wireOp",EDGE,"E35.trimOffspring"),sQuery(id+"F0.wireOp",EDGE,"E36.trimOffspring"),sQuery(id+"F0.wireOp",EDGE,"E37.trimOffspring"),sQuery(id+"F0.wireOp",EDGE,"E38.trimOffspring"),sQuery(id+"F0.wireOp",EDGE,"E39.trimOffspring"),sQuery(id+"F0.wireOp",EDGE,"E40.trimOffspring"),sQuery(id+"F0.wireOp",EDGE,"E41.trimOffspring"),sQuery(id+"F0.wireOp",EDGE,"E42.trimOffspring"),sQuery(id+"F0.wireOp",EDGE,"E43.trimOffspring"),sQuery(id+"F0.wireOp",EDGE,"E44.trimOffspring"),sQuery(id+"F0.wireOp",EDGE,"E45.trimOffspring"),sQuery(id+"F0.wireOp",EDGE,"E46.trimOffspring"),sQuery(id+"F0.wireOp",EDGE,"E47.trimOffspring"),sQuery(id+"F0.wireOp",EDGE,"E48.trimOffspring")])],"isStart":false});
            var sketch = newSketch(context, id + "F2", { "sketchPlane" : qUnion([Q0])});
            skCircle(sketch, "E49", {"center": v(0, 0) * mm, "radius": 3.18 * mm});
            skSolve(sketch);
        }
        {
            var Q0;
            Q0=qSketchRegion(id+"F2",true);
            extrude(context, id + "F3", {"entities" : qUnion([Q0]), "operationType" : NewBodyOperationType.REMOVE, "endBound" : BoundingType.THROUGH_ALL, "oppositeDirection" : true, "depth" : 25.4 * mm});
        }
    });
